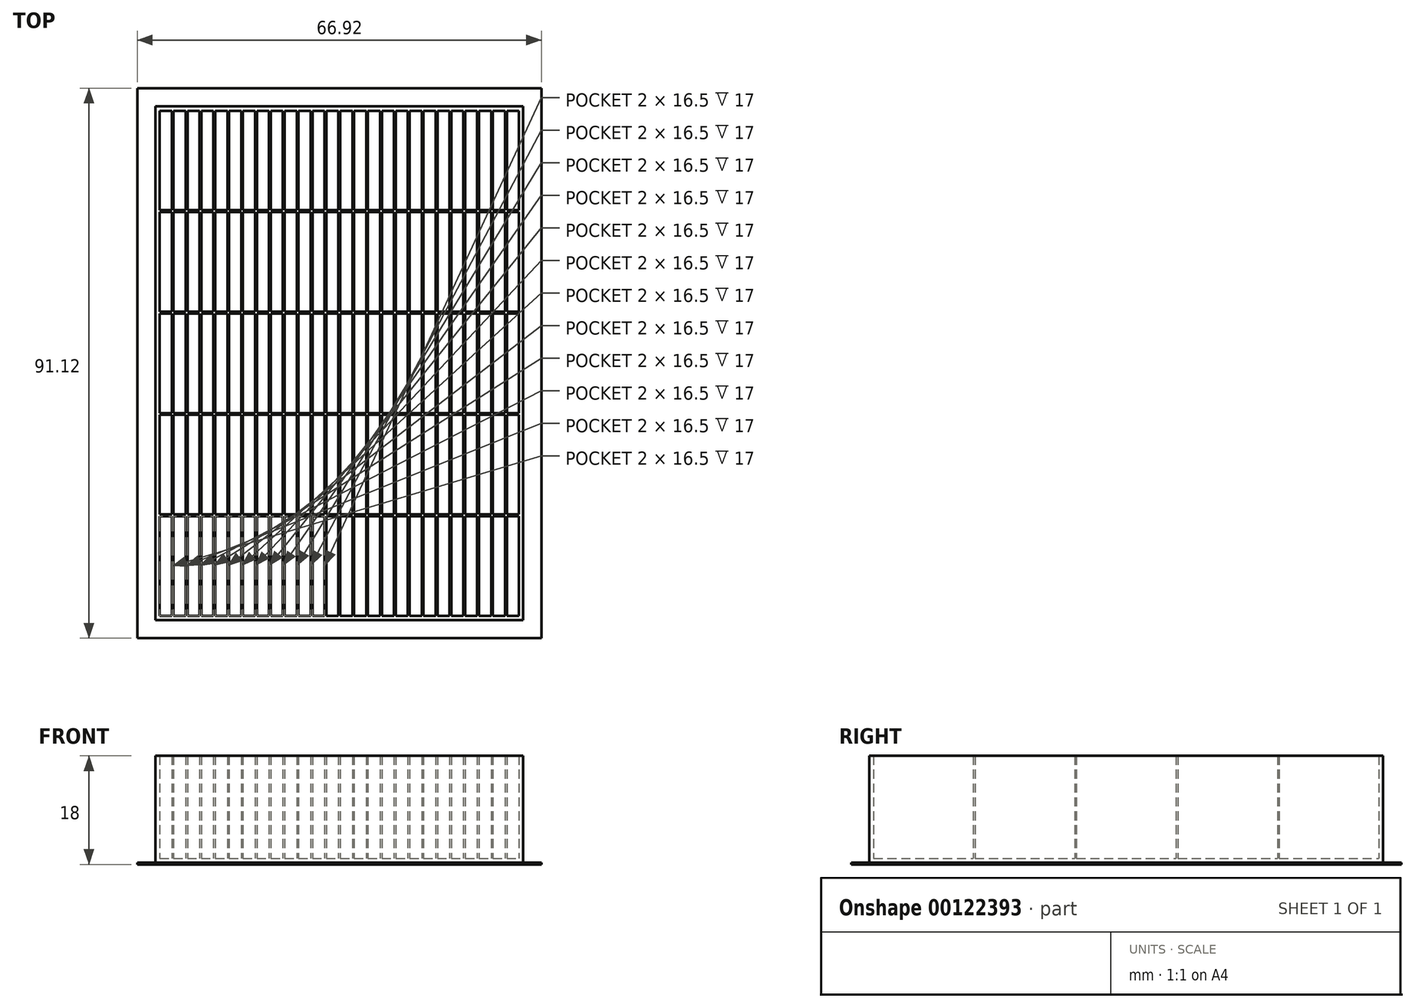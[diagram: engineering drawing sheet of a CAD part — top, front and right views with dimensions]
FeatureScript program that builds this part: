
annotation { "Feature Type Name" : "Feature", "Feature Type Description" : "" }
export const myFeature = defineFeature(function(context is Context, id is Id, definition is map)
    precondition{}
    {
        {
            var Q0;
            Q0=qCreatedBy(makeId("Top.planeOp"),FACE);
            var sketch = newSketch(context, id + "F0", { "sketchPlane" : qUnion([Q0])});
            skLineSegment(sketch, "E0.bottom", {"start": v(42.56, -30.46) * mm, "end": v(-42.56, -30.46) * mm});
            skLineSegment(sketch, "E0.top", {"start": v(42.56, 30.46) * mm, "end": v(-42.56, 30.46) * mm});
            skLineSegment(sketch, "E0.left", {"start": v(42.56, -30.46) * mm, "end": v(42.56, 30.46) * mm});
            skLineSegment(sketch, "E0.right", {"start": v(-42.56, -30.46) * mm, "end": v(-42.56, 30.46) * mm});
            skPoint(sketch, "E0.middle", {"position": v(0, 0) * mm});
            skLineSegment(sketch, "E1.bottom", {"start": v(-41.85, 29.75) * mm, "end": v(-25.35, 29.75) * mm});
            skLineSegment(sketch, "E1.top", {"start": v(-41.85, 27.75) * mm, "end": v(-25.35, 27.75) * mm});
            skLineSegment(sketch, "E1.left", {"start": v(-41.85, 29.75) * mm, "end": v(-41.85, 27.75) * mm});
            skLineSegment(sketch, "E1.right", {"start": v(-25.35, 29.75) * mm, "end": v(-25.35, 27.75) * mm});
            skLineSegment(sketch, "E2.0.1.0", {"start": v(-41.85, 27.45) * mm, "end": v(-41.85, 25.45) * mm});
            skLineSegment(sketch, "E2.0.1.1", {"start": v(-41.85, 25.45) * mm, "end": v(-25.35, 25.45) * mm});
            skLineSegment(sketch, "E2.0.1.2", {"start": v(-41.85, 27.45) * mm, "end": v(-25.35, 27.45) * mm});
            skLineSegment(sketch, "E2.0.1.3", {"start": v(-25.35, 27.45) * mm, "end": v(-25.35, 25.45) * mm});
            skLineSegment(sketch, "E2.0.2.0", {"start": v(-41.85, 25.15) * mm, "end": v(-41.85, 23.15) * mm});
            skLineSegment(sketch, "E2.0.2.1", {"start": v(-41.85, 23.15) * mm, "end": v(-25.35, 23.15) * mm});
            skLineSegment(sketch, "E2.0.2.2", {"start": v(-41.85, 25.15) * mm, "end": v(-25.35, 25.15) * mm});
            skLineSegment(sketch, "E2.0.2.3", {"start": v(-25.35, 25.15) * mm, "end": v(-25.35, 23.15) * mm});
            skLineSegment(sketch, "E2.0.3.0", {"start": v(-41.85, 22.85) * mm, "end": v(-41.85, 20.85) * mm});
            skLineSegment(sketch, "E2.0.3.1", {"start": v(-41.85, 20.85) * mm, "end": v(-25.35, 20.85) * mm});
            skLineSegment(sketch, "E2.0.3.2", {"start": v(-41.85, 22.85) * mm, "end": v(-25.35, 22.85) * mm});
            skLineSegment(sketch, "E2.0.3.3", {"start": v(-25.35, 22.85) * mm, "end": v(-25.35, 20.85) * mm});
            skLineSegment(sketch, "E2.0.4.0", {"start": v(-41.85, 20.55) * mm, "end": v(-41.85, 18.55) * mm});
            skLineSegment(sketch, "E2.0.4.1", {"start": v(-41.85, 18.55) * mm, "end": v(-25.35, 18.55) * mm});
            skLineSegment(sketch, "E2.0.4.2", {"start": v(-41.85, 20.55) * mm, "end": v(-25.35, 20.55) * mm});
            skLineSegment(sketch, "E2.0.4.3", {"start": v(-25.35, 20.55) * mm, "end": v(-25.35, 18.55) * mm});
            skLineSegment(sketch, "E2.0.5.0", {"start": v(-41.85, 18.25) * mm, "end": v(-41.85, 16.25) * mm});
            skLineSegment(sketch, "E2.0.5.1", {"start": v(-41.85, 16.25) * mm, "end": v(-25.35, 16.25) * mm});
            skLineSegment(sketch, "E2.0.5.2", {"start": v(-41.85, 18.25) * mm, "end": v(-25.35, 18.25) * mm});
            skLineSegment(sketch, "E2.0.5.3", {"start": v(-25.35, 18.25) * mm, "end": v(-25.35, 16.25) * mm});
            skLineSegment(sketch, "E2.0.6.0", {"start": v(-41.85, 15.95) * mm, "end": v(-41.85, 13.95) * mm});
            skLineSegment(sketch, "E2.0.6.1", {"start": v(-41.85, 13.95) * mm, "end": v(-25.35, 13.95) * mm});
            skLineSegment(sketch, "E2.0.6.2", {"start": v(-41.85, 15.95) * mm, "end": v(-25.35, 15.95) * mm});
            skLineSegment(sketch, "E2.0.6.3", {"start": v(-25.35, 15.95) * mm, "end": v(-25.35, 13.95) * mm});
            skLineSegment(sketch, "E2.0.7.0", {"start": v(-41.85, 13.65) * mm, "end": v(-41.85, 11.65) * mm});
            skLineSegment(sketch, "E2.0.7.1", {"start": v(-41.85, 11.65) * mm, "end": v(-25.35, 11.65) * mm});
            skLineSegment(sketch, "E2.0.7.2", {"start": v(-41.85, 13.65) * mm, "end": v(-25.35, 13.65) * mm});
            skLineSegment(sketch, "E2.0.7.3", {"start": v(-25.35, 13.65) * mm, "end": v(-25.35, 11.65) * mm});
            skLineSegment(sketch, "E2.0.8.0", {"start": v(-41.85, 11.35) * mm, "end": v(-41.85, 9.35) * mm});
            skLineSegment(sketch, "E2.0.8.1", {"start": v(-41.85, 9.35) * mm, "end": v(-25.35, 9.35) * mm});
            skLineSegment(sketch, "E2.0.8.2", {"start": v(-41.85, 11.35) * mm, "end": v(-25.35, 11.35) * mm});
            skLineSegment(sketch, "E2.0.8.3", {"start": v(-25.35, 11.35) * mm, "end": v(-25.35, 9.35) * mm});
            skLineSegment(sketch, "E2.0.9.0", {"start": v(-41.85, 9.05) * mm, "end": v(-41.85, 7.05) * mm});
            skLineSegment(sketch, "E2.0.9.1", {"start": v(-41.85, 7.05) * mm, "end": v(-25.35, 7.05) * mm});
            skLineSegment(sketch, "E2.0.9.2", {"start": v(-41.85, 9.05) * mm, "end": v(-25.35, 9.05) * mm});
            skLineSegment(sketch, "E2.0.9.3", {"start": v(-25.35, 9.05) * mm, "end": v(-25.35, 7.05) * mm});
            skLineSegment(sketch, "E2.0.10.0", {"start": v(-41.85, 6.75) * mm, "end": v(-41.85, 4.75) * mm});
            skLineSegment(sketch, "E2.0.10.1", {"start": v(-41.85, 4.75) * mm, "end": v(-25.35, 4.75) * mm});
            skLineSegment(sketch, "E2.0.10.2", {"start": v(-41.85, 6.75) * mm, "end": v(-25.35, 6.75) * mm});
            skLineSegment(sketch, "E2.0.10.3", {"start": v(-25.35, 6.75) * mm, "end": v(-25.35, 4.75) * mm});
            skLineSegment(sketch, "E2.0.11.0", {"start": v(-41.85, 4.45) * mm, "end": v(-41.85, 2.45) * mm});
            skLineSegment(sketch, "E2.0.11.1", {"start": v(-41.85, 2.45) * mm, "end": v(-25.35, 2.45) * mm});
            skLineSegment(sketch, "E2.0.11.2", {"start": v(-41.85, 4.45) * mm, "end": v(-25.35, 4.45) * mm});
            skLineSegment(sketch, "E2.0.11.3", {"start": v(-25.35, 4.45) * mm, "end": v(-25.35, 2.45) * mm});
            skLineSegment(sketch, "E2.0.12.0", {"start": v(-41.85, 2.15) * mm, "end": v(-41.85, 0.15) * mm});
            skLineSegment(sketch, "E2.0.12.1", {"start": v(-41.85, 0.15) * mm, "end": v(-25.35, 0.15) * mm});
            skLineSegment(sketch, "E2.0.12.2", {"start": v(-41.85, 2.15) * mm, "end": v(-25.35, 2.15) * mm});
            skLineSegment(sketch, "E2.0.12.3", {"start": v(-25.35, 2.15) * mm, "end": v(-25.35, 0.15) * mm});
            skLineSegment(sketch, "E2.0.13.0", {"start": v(-41.85, -0.15) * mm, "end": v(-41.85, -2.15) * mm});
            skLineSegment(sketch, "E2.0.13.1", {"start": v(-41.85, -2.15) * mm, "end": v(-25.35, -2.15) * mm});
            skLineSegment(sketch, "E2.0.13.2", {"start": v(-41.85, -0.15) * mm, "end": v(-25.35, -0.15) * mm});
            skLineSegment(sketch, "E2.0.13.3", {"start": v(-25.35, -0.15) * mm, "end": v(-25.35, -2.15) * mm});
            skLineSegment(sketch, "E2.0.14.0", {"start": v(-41.85, -2.45) * mm, "end": v(-41.85, -4.45) * mm});
            skLineSegment(sketch, "E2.0.14.1", {"start": v(-41.85, -4.45) * mm, "end": v(-25.35, -4.45) * mm});
            skLineSegment(sketch, "E2.0.14.2", {"start": v(-41.85, -2.45) * mm, "end": v(-25.35, -2.45) * mm});
            skLineSegment(sketch, "E2.0.14.3", {"start": v(-25.35, -2.45) * mm, "end": v(-25.35, -4.45) * mm});
            skLineSegment(sketch, "E2.0.15.0", {"start": v(-41.85, -4.75) * mm, "end": v(-41.85, -6.75) * mm});
            skLineSegment(sketch, "E2.0.15.1", {"start": v(-41.85, -6.75) * mm, "end": v(-25.35, -6.75) * mm});
            skLineSegment(sketch, "E2.0.15.2", {"start": v(-41.85, -4.75) * mm, "end": v(-25.35, -4.75) * mm});
            skLineSegment(sketch, "E2.0.15.3", {"start": v(-25.35, -4.75) * mm, "end": v(-25.35, -6.75) * mm});
            skLineSegment(sketch, "E2.0.16.0", {"start": v(-41.85, -7.05) * mm, "end": v(-41.85, -9.05) * mm});
            skLineSegment(sketch, "E2.0.16.1", {"start": v(-41.85, -9.05) * mm, "end": v(-25.35, -9.05) * mm});
            skLineSegment(sketch, "E2.0.16.2", {"start": v(-41.85, -7.05) * mm, "end": v(-25.35, -7.05) * mm});
            skLineSegment(sketch, "E2.0.16.3", {"start": v(-25.35, -7.05) * mm, "end": v(-25.35, -9.05) * mm});
            skLineSegment(sketch, "E2.0.17.0", {"start": v(-41.85, -9.35) * mm, "end": v(-41.85, -11.35) * mm});
            skLineSegment(sketch, "E2.0.17.1", {"start": v(-41.85, -11.35) * mm, "end": v(-25.35, -11.35) * mm});
            skLineSegment(sketch, "E2.0.17.2", {"start": v(-41.85, -9.35) * mm, "end": v(-25.35, -9.35) * mm});
            skLineSegment(sketch, "E2.0.17.3", {"start": v(-25.35, -9.35) * mm, "end": v(-25.35, -11.35) * mm});
            skLineSegment(sketch, "E2.0.18.0", {"start": v(-41.85, -11.65) * mm, "end": v(-41.85, -13.65) * mm});
            skLineSegment(sketch, "E2.0.18.1", {"start": v(-41.85, -13.65) * mm, "end": v(-25.35, -13.65) * mm});
            skLineSegment(sketch, "E2.0.18.2", {"start": v(-41.85, -11.65) * mm, "end": v(-25.35, -11.65) * mm});
            skLineSegment(sketch, "E2.0.18.3", {"start": v(-25.35, -11.65) * mm, "end": v(-25.35, -13.65) * mm});
            skLineSegment(sketch, "E2.0.19.0", {"start": v(-41.85, -13.95) * mm, "end": v(-41.85, -15.95) * mm});
            skLineSegment(sketch, "E2.0.19.1", {"start": v(-41.85, -15.95) * mm, "end": v(-25.35, -15.95) * mm});
            skLineSegment(sketch, "E2.0.19.2", {"start": v(-41.85, -13.95) * mm, "end": v(-25.35, -13.95) * mm});
            skLineSegment(sketch, "E2.0.19.3", {"start": v(-25.35, -13.95) * mm, "end": v(-25.35, -15.95) * mm});
            skLineSegment(sketch, "E2.0.20.0", {"start": v(-41.85, -16.25) * mm, "end": v(-41.85, -18.25) * mm});
            skLineSegment(sketch, "E2.0.20.1", {"start": v(-41.85, -18.25) * mm, "end": v(-25.35, -18.25) * mm});
            skLineSegment(sketch, "E2.0.20.2", {"start": v(-41.85, -16.25) * mm, "end": v(-25.35, -16.25) * mm});
            skLineSegment(sketch, "E2.0.20.3", {"start": v(-25.35, -16.25) * mm, "end": v(-25.35, -18.25) * mm});
            skLineSegment(sketch, "E2.0.21.0", {"start": v(-41.85, -18.55) * mm, "end": v(-41.85, -20.55) * mm});
            skLineSegment(sketch, "E2.0.21.1", {"start": v(-41.85, -20.55) * mm, "end": v(-25.35, -20.55) * mm});
            skLineSegment(sketch, "E2.0.21.2", {"start": v(-41.85, -18.55) * mm, "end": v(-25.35, -18.55) * mm});
            skLineSegment(sketch, "E2.0.21.3", {"start": v(-25.35, -18.55) * mm, "end": v(-25.35, -20.55) * mm});
            skLineSegment(sketch, "E2.0.22.0", {"start": v(-41.85, -20.85) * mm, "end": v(-41.85, -22.85) * mm});
            skLineSegment(sketch, "E2.0.22.1", {"start": v(-41.85, -22.85) * mm, "end": v(-25.35, -22.85) * mm});
            skLineSegment(sketch, "E2.0.22.2", {"start": v(-41.85, -20.85) * mm, "end": v(-25.35, -20.85) * mm});
            skLineSegment(sketch, "E2.0.22.3", {"start": v(-25.35, -20.85) * mm, "end": v(-25.35, -22.85) * mm});
            skLineSegment(sketch, "E2.0.23.0", {"start": v(-41.85, -23.15) * mm, "end": v(-41.85, -25.15) * mm});
            skLineSegment(sketch, "E2.0.23.1", {"start": v(-41.85, -25.15) * mm, "end": v(-25.35, -25.15) * mm});
            skLineSegment(sketch, "E2.0.23.2", {"start": v(-41.85, -23.15) * mm, "end": v(-25.35, -23.15) * mm});
            skLineSegment(sketch, "E2.0.23.3", {"start": v(-25.35, -23.15) * mm, "end": v(-25.35, -25.15) * mm});
            skLineSegment(sketch, "E2.0.24.0", {"start": v(-41.85, -25.45) * mm, "end": v(-41.85, -27.45) * mm});
            skLineSegment(sketch, "E2.0.24.1", {"start": v(-41.85, -27.45) * mm, "end": v(-25.35, -27.45) * mm});
            skLineSegment(sketch, "E2.0.24.2", {"start": v(-41.85, -25.45) * mm, "end": v(-25.35, -25.45) * mm});
            skLineSegment(sketch, "E2.0.24.3", {"start": v(-25.35, -25.45) * mm, "end": v(-25.35, -27.45) * mm});
            skLineSegment(sketch, "E2.0.25.0", {"start": v(-41.85, -27.75) * mm, "end": v(-41.85, -29.75) * mm});
            skLineSegment(sketch, "E2.0.25.1", {"start": v(-41.85, -29.75) * mm, "end": v(-25.35, -29.75) * mm});
            skLineSegment(sketch, "E2.0.25.2", {"start": v(-41.85, -27.75) * mm, "end": v(-25.35, -27.75) * mm});
            skLineSegment(sketch, "E2.0.25.3", {"start": v(-25.35, -27.75) * mm, "end": v(-25.35, -29.75) * mm});
            skLineSegment(sketch, "E2.1.0.0", {"start": v(-25.05, 29.75) * mm, "end": v(-25.05, 27.75) * mm});
            skLineSegment(sketch, "E2.1.0.1", {"start": v(-25.05, 27.75) * mm, "end": v(-8.55, 27.75) * mm});
            skLineSegment(sketch, "E2.1.0.2", {"start": v(-25.05, 29.75) * mm, "end": v(-8.55, 29.75) * mm});
            skLineSegment(sketch, "E2.1.0.3", {"start": v(-8.55, 29.75) * mm, "end": v(-8.55, 27.75) * mm});
            skLineSegment(sketch, "E2.1.1.0", {"start": v(-25.05, 27.45) * mm, "end": v(-25.05, 25.45) * mm});
            skLineSegment(sketch, "E2.1.1.1", {"start": v(-25.05, 25.45) * mm, "end": v(-8.55, 25.45) * mm});
            skLineSegment(sketch, "E2.1.1.2", {"start": v(-25.05, 27.45) * mm, "end": v(-8.55, 27.45) * mm});
            skLineSegment(sketch, "E2.1.1.3", {"start": v(-8.55, 27.45) * mm, "end": v(-8.55, 25.45) * mm});
            skLineSegment(sketch, "E2.1.2.0", {"start": v(-25.05, 25.15) * mm, "end": v(-25.05, 23.15) * mm});
            skLineSegment(sketch, "E2.1.2.1", {"start": v(-25.05, 23.15) * mm, "end": v(-8.55, 23.15) * mm});
            skLineSegment(sketch, "E2.1.2.2", {"start": v(-25.05, 25.15) * mm, "end": v(-8.55, 25.15) * mm});
            skLineSegment(sketch, "E2.1.2.3", {"start": v(-8.55, 25.15) * mm, "end": v(-8.55, 23.15) * mm});
            skLineSegment(sketch, "E2.1.3.0", {"start": v(-25.05, 22.85) * mm, "end": v(-25.05, 20.85) * mm});
            skLineSegment(sketch, "E2.1.3.1", {"start": v(-25.05, 20.85) * mm, "end": v(-8.55, 20.85) * mm});
            skLineSegment(sketch, "E2.1.3.2", {"start": v(-25.05, 22.85) * mm, "end": v(-8.55, 22.85) * mm});
            skLineSegment(sketch, "E2.1.3.3", {"start": v(-8.55, 22.85) * mm, "end": v(-8.55, 20.85) * mm});
            skLineSegment(sketch, "E2.1.4.0", {"start": v(-25.05, 20.55) * mm, "end": v(-25.05, 18.55) * mm});
            skLineSegment(sketch, "E2.1.4.1", {"start": v(-25.05, 18.55) * mm, "end": v(-8.55, 18.55) * mm});
            skLineSegment(sketch, "E2.1.4.2", {"start": v(-25.05, 20.55) * mm, "end": v(-8.55, 20.55) * mm});
            skLineSegment(sketch, "E2.1.4.3", {"start": v(-8.55, 20.55) * mm, "end": v(-8.55, 18.55) * mm});
            skLineSegment(sketch, "E2.1.5.0", {"start": v(-25.05, 18.25) * mm, "end": v(-25.05, 16.25) * mm});
            skLineSegment(sketch, "E2.1.5.1", {"start": v(-25.05, 16.25) * mm, "end": v(-8.55, 16.25) * mm});
            skLineSegment(sketch, "E2.1.5.2", {"start": v(-25.05, 18.25) * mm, "end": v(-8.55, 18.25) * mm});
            skLineSegment(sketch, "E2.1.5.3", {"start": v(-8.55, 18.25) * mm, "end": v(-8.55, 16.25) * mm});
            skLineSegment(sketch, "E2.1.6.0", {"start": v(-25.05, 15.95) * mm, "end": v(-25.05, 13.95) * mm});
            skLineSegment(sketch, "E2.1.6.1", {"start": v(-25.05, 13.95) * mm, "end": v(-8.55, 13.95) * mm});
            skLineSegment(sketch, "E2.1.6.2", {"start": v(-25.05, 15.95) * mm, "end": v(-8.55, 15.95) * mm});
            skLineSegment(sketch, "E2.1.6.3", {"start": v(-8.55, 15.95) * mm, "end": v(-8.55, 13.95) * mm});
            skLineSegment(sketch, "E2.1.7.0", {"start": v(-25.05, 13.65) * mm, "end": v(-25.05, 11.65) * mm});
            skLineSegment(sketch, "E2.1.7.1", {"start": v(-25.05, 11.65) * mm, "end": v(-8.55, 11.65) * mm});
            skLineSegment(sketch, "E2.1.7.2", {"start": v(-25.05, 13.65) * mm, "end": v(-8.55, 13.65) * mm});
            skLineSegment(sketch, "E2.1.7.3", {"start": v(-8.55, 13.65) * mm, "end": v(-8.55, 11.65) * mm});
            skLineSegment(sketch, "E2.1.8.0", {"start": v(-25.05, 11.35) * mm, "end": v(-25.05, 9.35) * mm});
            skLineSegment(sketch, "E2.1.8.1", {"start": v(-25.05, 9.35) * mm, "end": v(-8.55, 9.35) * mm});
            skLineSegment(sketch, "E2.1.8.2", {"start": v(-25.05, 11.35) * mm, "end": v(-8.55, 11.35) * mm});
            skLineSegment(sketch, "E2.1.8.3", {"start": v(-8.55, 11.35) * mm, "end": v(-8.55, 9.35) * mm});
            skLineSegment(sketch, "E2.1.9.0", {"start": v(-25.05, 9.05) * mm, "end": v(-25.05, 7.05) * mm});
            skLineSegment(sketch, "E2.1.9.1", {"start": v(-25.05, 7.05) * mm, "end": v(-8.55, 7.05) * mm});
            skLineSegment(sketch, "E2.1.9.2", {"start": v(-25.05, 9.05) * mm, "end": v(-8.55, 9.05) * mm});
            skLineSegment(sketch, "E2.1.9.3", {"start": v(-8.55, 9.05) * mm, "end": v(-8.55, 7.05) * mm});
            skLineSegment(sketch, "E2.1.10.0", {"start": v(-25.05, 6.75) * mm, "end": v(-25.05, 4.75) * mm});
            skLineSegment(sketch, "E2.1.10.1", {"start": v(-25.05, 4.75) * mm, "end": v(-8.55, 4.75) * mm});
            skLineSegment(sketch, "E2.1.10.2", {"start": v(-25.05, 6.75) * mm, "end": v(-8.55, 6.75) * mm});
            skLineSegment(sketch, "E2.1.10.3", {"start": v(-8.55, 6.75) * mm, "end": v(-8.55, 4.75) * mm});
            skLineSegment(sketch, "E2.1.11.0", {"start": v(-25.05, 4.45) * mm, "end": v(-25.05, 2.45) * mm});
            skLineSegment(sketch, "E2.1.11.1", {"start": v(-25.05, 2.45) * mm, "end": v(-8.55, 2.45) * mm});
            skLineSegment(sketch, "E2.1.11.2", {"start": v(-25.05, 4.45) * mm, "end": v(-8.55, 4.45) * mm});
            skLineSegment(sketch, "E2.1.11.3", {"start": v(-8.55, 4.45) * mm, "end": v(-8.55, 2.45) * mm});
            skLineSegment(sketch, "E2.1.12.0", {"start": v(-25.05, 2.15) * mm, "end": v(-25.05, 0.15) * mm});
            skLineSegment(sketch, "E2.1.12.1", {"start": v(-25.05, 0.15) * mm, "end": v(-8.55, 0.15) * mm});
            skLineSegment(sketch, "E2.1.12.2", {"start": v(-25.05, 2.15) * mm, "end": v(-8.55, 2.15) * mm});
            skLineSegment(sketch, "E2.1.12.3", {"start": v(-8.55, 2.15) * mm, "end": v(-8.55, 0.15) * mm});
            skLineSegment(sketch, "E2.1.13.0", {"start": v(-25.05, -0.15) * mm, "end": v(-25.05, -2.15) * mm});
            skLineSegment(sketch, "E2.1.13.1", {"start": v(-25.05, -2.15) * mm, "end": v(-8.55, -2.15) * mm});
            skLineSegment(sketch, "E2.1.13.2", {"start": v(-25.05, -0.15) * mm, "end": v(-8.55, -0.15) * mm});
            skLineSegment(sketch, "E2.1.13.3", {"start": v(-8.55, -0.15) * mm, "end": v(-8.55, -2.15) * mm});
            skLineSegment(sketch, "E2.1.14.0", {"start": v(-25.05, -2.45) * mm, "end": v(-25.05, -4.45) * mm});
            skLineSegment(sketch, "E2.1.14.1", {"start": v(-25.05, -4.45) * mm, "end": v(-8.55, -4.45) * mm});
            skLineSegment(sketch, "E2.1.14.2", {"start": v(-25.05, -2.45) * mm, "end": v(-8.55, -2.45) * mm});
            skLineSegment(sketch, "E2.1.14.3", {"start": v(-8.55, -2.45) * mm, "end": v(-8.55, -4.45) * mm});
            skLineSegment(sketch, "E2.1.15.0", {"start": v(-25.05, -4.75) * mm, "end": v(-25.05, -6.75) * mm});
            skLineSegment(sketch, "E2.1.15.1", {"start": v(-25.05, -6.75) * mm, "end": v(-8.55, -6.75) * mm});
            skLineSegment(sketch, "E2.1.15.2", {"start": v(-25.05, -4.75) * mm, "end": v(-8.55, -4.75) * mm});
            skLineSegment(sketch, "E2.1.15.3", {"start": v(-8.55, -4.75) * mm, "end": v(-8.55, -6.75) * mm});
            skLineSegment(sketch, "E2.1.16.0", {"start": v(-25.05, -7.05) * mm, "end": v(-25.05, -9.05) * mm});
            skLineSegment(sketch, "E2.1.16.1", {"start": v(-25.05, -9.05) * mm, "end": v(-8.55, -9.05) * mm});
            skLineSegment(sketch, "E2.1.16.2", {"start": v(-25.05, -7.05) * mm, "end": v(-8.55, -7.05) * mm});
            skLineSegment(sketch, "E2.1.16.3", {"start": v(-8.55, -7.05) * mm, "end": v(-8.55, -9.05) * mm});
            skLineSegment(sketch, "E2.1.17.0", {"start": v(-25.05, -9.35) * mm, "end": v(-25.05, -11.35) * mm});
            skLineSegment(sketch, "E2.1.17.1", {"start": v(-25.05, -11.35) * mm, "end": v(-8.55, -11.35) * mm});
            skLineSegment(sketch, "E2.1.17.2", {"start": v(-25.05, -9.35) * mm, "end": v(-8.55, -9.35) * mm});
            skLineSegment(sketch, "E2.1.17.3", {"start": v(-8.55, -9.35) * mm, "end": v(-8.55, -11.35) * mm});
            skLineSegment(sketch, "E2.1.18.0", {"start": v(-25.05, -11.65) * mm, "end": v(-25.05, -13.65) * mm});
            skLineSegment(sketch, "E2.1.18.1", {"start": v(-25.05, -13.65) * mm, "end": v(-8.55, -13.65) * mm});
            skLineSegment(sketch, "E2.1.18.2", {"start": v(-25.05, -11.65) * mm, "end": v(-8.55, -11.65) * mm});
            skLineSegment(sketch, "E2.1.18.3", {"start": v(-8.55, -11.65) * mm, "end": v(-8.55, -13.65) * mm});
            skLineSegment(sketch, "E2.1.19.0", {"start": v(-25.05, -13.95) * mm, "end": v(-25.05, -15.95) * mm});
            skLineSegment(sketch, "E2.1.19.1", {"start": v(-25.05, -15.95) * mm, "end": v(-8.55, -15.95) * mm});
            skLineSegment(sketch, "E2.1.19.2", {"start": v(-25.05, -13.95) * mm, "end": v(-8.55, -13.95) * mm});
            skLineSegment(sketch, "E2.1.19.3", {"start": v(-8.55, -13.95) * mm, "end": v(-8.55, -15.95) * mm});
            skLineSegment(sketch, "E2.1.20.0", {"start": v(-25.05, -16.25) * mm, "end": v(-25.05, -18.25) * mm});
            skLineSegment(sketch, "E2.1.20.1", {"start": v(-25.05, -18.25) * mm, "end": v(-8.55, -18.25) * mm});
            skLineSegment(sketch, "E2.1.20.2", {"start": v(-25.05, -16.25) * mm, "end": v(-8.55, -16.25) * mm});
            skLineSegment(sketch, "E2.1.20.3", {"start": v(-8.55, -16.25) * mm, "end": v(-8.55, -18.25) * mm});
            skLineSegment(sketch, "E2.1.21.0", {"start": v(-25.05, -18.55) * mm, "end": v(-25.05, -20.55) * mm});
            skLineSegment(sketch, "E2.1.21.1", {"start": v(-25.05, -20.55) * mm, "end": v(-8.55, -20.55) * mm});
            skLineSegment(sketch, "E2.1.21.2", {"start": v(-25.05, -18.55) * mm, "end": v(-8.55, -18.55) * mm});
            skLineSegment(sketch, "E2.1.21.3", {"start": v(-8.55, -18.55) * mm, "end": v(-8.55, -20.55) * mm});
            skLineSegment(sketch, "E2.1.22.0", {"start": v(-25.05, -20.85) * mm, "end": v(-25.05, -22.85) * mm});
            skLineSegment(sketch, "E2.1.22.1", {"start": v(-25.05, -22.85) * mm, "end": v(-8.55, -22.85) * mm});
            skLineSegment(sketch, "E2.1.22.2", {"start": v(-25.05, -20.85) * mm, "end": v(-8.55, -20.85) * mm});
            skLineSegment(sketch, "E2.1.22.3", {"start": v(-8.55, -20.85) * mm, "end": v(-8.55, -22.85) * mm});
            skLineSegment(sketch, "E2.1.23.0", {"start": v(-25.05, -23.15) * mm, "end": v(-25.05, -25.15) * mm});
            skLineSegment(sketch, "E2.1.23.1", {"start": v(-25.05, -25.15) * mm, "end": v(-8.55, -25.15) * mm});
            skLineSegment(sketch, "E2.1.23.2", {"start": v(-25.05, -23.15) * mm, "end": v(-8.55, -23.15) * mm});
            skLineSegment(sketch, "E2.1.23.3", {"start": v(-8.55, -23.15) * mm, "end": v(-8.55, -25.15) * mm});
            skLineSegment(sketch, "E2.1.24.0", {"start": v(-25.05, -25.45) * mm, "end": v(-25.05, -27.45) * mm});
            skLineSegment(sketch, "E2.1.24.1", {"start": v(-25.05, -27.45) * mm, "end": v(-8.55, -27.45) * mm});
            skLineSegment(sketch, "E2.1.24.2", {"start": v(-25.05, -25.45) * mm, "end": v(-8.55, -25.45) * mm});
            skLineSegment(sketch, "E2.1.24.3", {"start": v(-8.55, -25.45) * mm, "end": v(-8.55, -27.45) * mm});
            skLineSegment(sketch, "E2.1.25.0", {"start": v(-25.05, -27.75) * mm, "end": v(-25.05, -29.75) * mm});
            skLineSegment(sketch, "E2.1.25.1", {"start": v(-25.05, -29.75) * mm, "end": v(-8.55, -29.75) * mm});
            skLineSegment(sketch, "E2.1.25.2", {"start": v(-25.05, -27.75) * mm, "end": v(-8.55, -27.75) * mm});
            skLineSegment(sketch, "E2.1.25.3", {"start": v(-8.55, -27.75) * mm, "end": v(-8.55, -29.75) * mm});
            skLineSegment(sketch, "E2.2.0.0", {"start": v(-8.25, 29.75) * mm, "end": v(-8.25, 27.75) * mm});
            skLineSegment(sketch, "E2.2.0.1", {"start": v(-8.25, 27.75) * mm, "end": v(8.25, 27.75) * mm});
            skLineSegment(sketch, "E2.2.0.2", {"start": v(-8.25, 29.75) * mm, "end": v(8.25, 29.75) * mm});
            skLineSegment(sketch, "E2.2.0.3", {"start": v(8.25, 29.75) * mm, "end": v(8.25, 27.75) * mm});
            skLineSegment(sketch, "E2.2.1.0", {"start": v(-8.25, 27.45) * mm, "end": v(-8.25, 25.45) * mm});
            skLineSegment(sketch, "E2.2.1.1", {"start": v(-8.25, 25.45) * mm, "end": v(8.25, 25.45) * mm});
            skLineSegment(sketch, "E2.2.1.2", {"start": v(-8.25, 27.45) * mm, "end": v(8.25, 27.45) * mm});
            skLineSegment(sketch, "E2.2.1.3", {"start": v(8.25, 27.45) * mm, "end": v(8.25, 25.45) * mm});
            skLineSegment(sketch, "E2.2.2.0", {"start": v(-8.25, 25.15) * mm, "end": v(-8.25, 23.15) * mm});
            skLineSegment(sketch, "E2.2.2.1", {"start": v(-8.25, 23.15) * mm, "end": v(8.25, 23.15) * mm});
            skLineSegment(sketch, "E2.2.2.2", {"start": v(-8.25, 25.15) * mm, "end": v(8.25, 25.15) * mm});
            skLineSegment(sketch, "E2.2.2.3", {"start": v(8.25, 25.15) * mm, "end": v(8.25, 23.15) * mm});
            skLineSegment(sketch, "E2.2.3.0", {"start": v(-8.25, 22.85) * mm, "end": v(-8.25, 20.85) * mm});
            skLineSegment(sketch, "E2.2.3.1", {"start": v(-8.25, 20.85) * mm, "end": v(8.25, 20.85) * mm});
            skLineSegment(sketch, "E2.2.3.2", {"start": v(-8.25, 22.85) * mm, "end": v(8.25, 22.85) * mm});
            skLineSegment(sketch, "E2.2.3.3", {"start": v(8.25, 22.85) * mm, "end": v(8.25, 20.85) * mm});
            skLineSegment(sketch, "E2.2.4.0", {"start": v(-8.25, 20.55) * mm, "end": v(-8.25, 18.55) * mm});
            skLineSegment(sketch, "E2.2.4.1", {"start": v(-8.25, 18.55) * mm, "end": v(8.25, 18.55) * mm});
            skLineSegment(sketch, "E2.2.4.2", {"start": v(-8.25, 20.55) * mm, "end": v(8.25, 20.55) * mm});
            skLineSegment(sketch, "E2.2.4.3", {"start": v(8.25, 20.55) * mm, "end": v(8.25, 18.55) * mm});
            skLineSegment(sketch, "E2.2.5.0", {"start": v(-8.25, 18.25) * mm, "end": v(-8.25, 16.25) * mm});
            skLineSegment(sketch, "E2.2.5.1", {"start": v(-8.25, 16.25) * mm, "end": v(8.25, 16.25) * mm});
            skLineSegment(sketch, "E2.2.5.2", {"start": v(-8.25, 18.25) * mm, "end": v(8.25, 18.25) * mm});
            skLineSegment(sketch, "E2.2.5.3", {"start": v(8.25, 18.25) * mm, "end": v(8.25, 16.25) * mm});
            skLineSegment(sketch, "E2.2.6.0", {"start": v(-8.25, 15.95) * mm, "end": v(-8.25, 13.95) * mm});
            skLineSegment(sketch, "E2.2.6.1", {"start": v(-8.25, 13.95) * mm, "end": v(8.25, 13.95) * mm});
            skLineSegment(sketch, "E2.2.6.2", {"start": v(-8.25, 15.95) * mm, "end": v(8.25, 15.95) * mm});
            skLineSegment(sketch, "E2.2.6.3", {"start": v(8.25, 15.95) * mm, "end": v(8.25, 13.95) * mm});
            skLineSegment(sketch, "E2.2.7.0", {"start": v(-8.25, 13.65) * mm, "end": v(-8.25, 11.65) * mm});
            skLineSegment(sketch, "E2.2.7.1", {"start": v(-8.25, 11.65) * mm, "end": v(8.25, 11.65) * mm});
            skLineSegment(sketch, "E2.2.7.2", {"start": v(-8.25, 13.65) * mm, "end": v(8.25, 13.65) * mm});
            skLineSegment(sketch, "E2.2.7.3", {"start": v(8.25, 13.65) * mm, "end": v(8.25, 11.65) * mm});
            skLineSegment(sketch, "E2.2.8.0", {"start": v(-8.25, 11.35) * mm, "end": v(-8.25, 9.35) * mm});
            skLineSegment(sketch, "E2.2.8.1", {"start": v(-8.25, 9.35) * mm, "end": v(8.25, 9.35) * mm});
            skLineSegment(sketch, "E2.2.8.2", {"start": v(-8.25, 11.35) * mm, "end": v(8.25, 11.35) * mm});
            skLineSegment(sketch, "E2.2.8.3", {"start": v(8.25, 11.35) * mm, "end": v(8.25, 9.35) * mm});
            skLineSegment(sketch, "E2.2.9.0", {"start": v(-8.25, 9.05) * mm, "end": v(-8.25, 7.05) * mm});
            skLineSegment(sketch, "E2.2.9.1", {"start": v(-8.25, 7.05) * mm, "end": v(8.25, 7.05) * mm});
            skLineSegment(sketch, "E2.2.9.2", {"start": v(-8.25, 9.05) * mm, "end": v(8.25, 9.05) * mm});
            skLineSegment(sketch, "E2.2.9.3", {"start": v(8.25, 9.05) * mm, "end": v(8.25, 7.05) * mm});
            skLineSegment(sketch, "E2.2.10.0", {"start": v(-8.25, 6.75) * mm, "end": v(-8.25, 4.75) * mm});
            skLineSegment(sketch, "E2.2.10.1", {"start": v(-8.25, 4.75) * mm, "end": v(8.25, 4.75) * mm});
            skLineSegment(sketch, "E2.2.10.2", {"start": v(-8.25, 6.75) * mm, "end": v(8.25, 6.75) * mm});
            skLineSegment(sketch, "E2.2.10.3", {"start": v(8.25, 6.75) * mm, "end": v(8.25, 4.75) * mm});
            skLineSegment(sketch, "E2.2.11.0", {"start": v(-8.25, 4.45) * mm, "end": v(-8.25, 2.45) * mm});
            skLineSegment(sketch, "E2.2.11.1", {"start": v(-8.25, 2.45) * mm, "end": v(8.25, 2.45) * mm});
            skLineSegment(sketch, "E2.2.11.2", {"start": v(-8.25, 4.45) * mm, "end": v(8.25, 4.45) * mm});
            skLineSegment(sketch, "E2.2.11.3", {"start": v(8.25, 4.45) * mm, "end": v(8.25, 2.45) * mm});
            skLineSegment(sketch, "E2.2.12.0", {"start": v(-8.25, 2.15) * mm, "end": v(-8.25, 0.15) * mm});
            skLineSegment(sketch, "E2.2.12.1", {"start": v(-8.25, 0.15) * mm, "end": v(8.25, 0.15) * mm});
            skLineSegment(sketch, "E2.2.12.2", {"start": v(-8.25, 2.15) * mm, "end": v(8.25, 2.15) * mm});
            skLineSegment(sketch, "E2.2.12.3", {"start": v(8.25, 2.15) * mm, "end": v(8.25, 0.15) * mm});
            skLineSegment(sketch, "E2.2.13.0", {"start": v(-8.25, -0.15) * mm, "end": v(-8.25, -2.15) * mm});
            skLineSegment(sketch, "E2.2.13.1", {"start": v(-8.25, -2.15) * mm, "end": v(8.25, -2.15) * mm});
            skLineSegment(sketch, "E2.2.13.2", {"start": v(-8.25, -0.15) * mm, "end": v(8.25, -0.15) * mm});
            skLineSegment(sketch, "E2.2.13.3", {"start": v(8.25, -0.15) * mm, "end": v(8.25, -2.15) * mm});
            skLineSegment(sketch, "E2.2.14.0", {"start": v(-8.25, -2.45) * mm, "end": v(-8.25, -4.45) * mm});
            skLineSegment(sketch, "E2.2.14.1", {"start": v(-8.25, -4.45) * mm, "end": v(8.25, -4.45) * mm});
            skLineSegment(sketch, "E2.2.14.2", {"start": v(-8.25, -2.45) * mm, "end": v(8.25, -2.45) * mm});
            skLineSegment(sketch, "E2.2.14.3", {"start": v(8.25, -2.45) * mm, "end": v(8.25, -4.45) * mm});
            skLineSegment(sketch, "E2.2.15.0", {"start": v(-8.25, -4.75) * mm, "end": v(-8.25, -6.75) * mm});
            skLineSegment(sketch, "E2.2.15.1", {"start": v(-8.25, -6.75) * mm, "end": v(8.25, -6.75) * mm});
            skLineSegment(sketch, "E2.2.15.2", {"start": v(-8.25, -4.75) * mm, "end": v(8.25, -4.75) * mm});
            skLineSegment(sketch, "E2.2.15.3", {"start": v(8.25, -4.75) * mm, "end": v(8.25, -6.75) * mm});
            skLineSegment(sketch, "E2.2.16.0", {"start": v(-8.25, -7.05) * mm, "end": v(-8.25, -9.05) * mm});
            skLineSegment(sketch, "E2.2.16.1", {"start": v(-8.25, -9.05) * mm, "end": v(8.25, -9.05) * mm});
            skLineSegment(sketch, "E2.2.16.2", {"start": v(-8.25, -7.05) * mm, "end": v(8.25, -7.05) * mm});
            skLineSegment(sketch, "E2.2.16.3", {"start": v(8.25, -7.05) * mm, "end": v(8.25, -9.05) * mm});
            skLineSegment(sketch, "E2.2.17.0", {"start": v(-8.25, -9.35) * mm, "end": v(-8.25, -11.35) * mm});
            skLineSegment(sketch, "E2.2.17.1", {"start": v(-8.25, -11.35) * mm, "end": v(8.25, -11.35) * mm});
            skLineSegment(sketch, "E2.2.17.2", {"start": v(-8.25, -9.35) * mm, "end": v(8.25, -9.35) * mm});
            skLineSegment(sketch, "E2.2.17.3", {"start": v(8.25, -9.35) * mm, "end": v(8.25, -11.35) * mm});
            skLineSegment(sketch, "E2.2.18.0", {"start": v(-8.25, -11.65) * mm, "end": v(-8.25, -13.65) * mm});
            skLineSegment(sketch, "E2.2.18.1", {"start": v(-8.25, -13.65) * mm, "end": v(8.25, -13.65) * mm});
            skLineSegment(sketch, "E2.2.18.2", {"start": v(-8.25, -11.65) * mm, "end": v(8.25, -11.65) * mm});
            skLineSegment(sketch, "E2.2.18.3", {"start": v(8.25, -11.65) * mm, "end": v(8.25, -13.65) * mm});
            skLineSegment(sketch, "E2.2.19.0", {"start": v(-8.25, -13.95) * mm, "end": v(-8.25, -15.95) * mm});
            skLineSegment(sketch, "E2.2.19.1", {"start": v(-8.25, -15.95) * mm, "end": v(8.25, -15.95) * mm});
            skLineSegment(sketch, "E2.2.19.2", {"start": v(-8.25, -13.95) * mm, "end": v(8.25, -13.95) * mm});
            skLineSegment(sketch, "E2.2.19.3", {"start": v(8.25, -13.95) * mm, "end": v(8.25, -15.95) * mm});
            skLineSegment(sketch, "E2.2.20.0", {"start": v(-8.25, -16.25) * mm, "end": v(-8.25, -18.25) * mm});
            skLineSegment(sketch, "E2.2.20.1", {"start": v(-8.25, -18.25) * mm, "end": v(8.25, -18.25) * mm});
            skLineSegment(sketch, "E2.2.20.2", {"start": v(-8.25, -16.25) * mm, "end": v(8.25, -16.25) * mm});
            skLineSegment(sketch, "E2.2.20.3", {"start": v(8.25, -16.25) * mm, "end": v(8.25, -18.25) * mm});
            skLineSegment(sketch, "E2.2.21.0", {"start": v(-8.25, -18.55) * mm, "end": v(-8.25, -20.55) * mm});
            skLineSegment(sketch, "E2.2.21.1", {"start": v(-8.25, -20.55) * mm, "end": v(8.25, -20.55) * mm});
            skLineSegment(sketch, "E2.2.21.2", {"start": v(-8.25, -18.55) * mm, "end": v(8.25, -18.55) * mm});
            skLineSegment(sketch, "E2.2.21.3", {"start": v(8.25, -18.55) * mm, "end": v(8.25, -20.55) * mm});
            skLineSegment(sketch, "E2.2.22.0", {"start": v(-8.25, -20.85) * mm, "end": v(-8.25, -22.85) * mm});
            skLineSegment(sketch, "E2.2.22.1", {"start": v(-8.25, -22.85) * mm, "end": v(8.25, -22.85) * mm});
            skLineSegment(sketch, "E2.2.22.2", {"start": v(-8.25, -20.85) * mm, "end": v(8.25, -20.85) * mm});
            skLineSegment(sketch, "E2.2.22.3", {"start": v(8.25, -20.85) * mm, "end": v(8.25, -22.85) * mm});
            skLineSegment(sketch, "E2.2.23.0", {"start": v(-8.25, -23.15) * mm, "end": v(-8.25, -25.15) * mm});
            skLineSegment(sketch, "E2.2.23.1", {"start": v(-8.25, -25.15) * mm, "end": v(8.25, -25.15) * mm});
            skLineSegment(sketch, "E2.2.23.2", {"start": v(-8.25, -23.15) * mm, "end": v(8.25, -23.15) * mm});
            skLineSegment(sketch, "E2.2.23.3", {"start": v(8.25, -23.15) * mm, "end": v(8.25, -25.15) * mm});
            skLineSegment(sketch, "E2.2.24.0", {"start": v(-8.25, -25.45) * mm, "end": v(-8.25, -27.45) * mm});
            skLineSegment(sketch, "E2.2.24.1", {"start": v(-8.25, -27.45) * mm, "end": v(8.25, -27.45) * mm});
            skLineSegment(sketch, "E2.2.24.2", {"start": v(-8.25, -25.45) * mm, "end": v(8.25, -25.45) * mm});
            skLineSegment(sketch, "E2.2.24.3", {"start": v(8.25, -25.45) * mm, "end": v(8.25, -27.45) * mm});
            skLineSegment(sketch, "E2.2.25.0", {"start": v(-8.25, -27.75) * mm, "end": v(-8.25, -29.75) * mm});
            skLineSegment(sketch, "E2.2.25.1", {"start": v(-8.25, -29.75) * mm, "end": v(8.25, -29.75) * mm});
            skLineSegment(sketch, "E2.2.25.2", {"start": v(-8.25, -27.75) * mm, "end": v(8.25, -27.75) * mm});
            skLineSegment(sketch, "E2.2.25.3", {"start": v(8.25, -27.75) * mm, "end": v(8.25, -29.75) * mm});
            skLineSegment(sketch, "E2.3.0.0", {"start": v(8.55, 29.75) * mm, "end": v(8.55, 27.75) * mm});
            skLineSegment(sketch, "E2.3.0.1", {"start": v(8.55, 27.75) * mm, "end": v(25.05, 27.75) * mm});
            skLineSegment(sketch, "E2.3.0.2", {"start": v(8.55, 29.75) * mm, "end": v(25.05, 29.75) * mm});
            skLineSegment(sketch, "E2.3.0.3", {"start": v(25.05, 29.75) * mm, "end": v(25.05, 27.75) * mm});
            skLineSegment(sketch, "E2.3.1.0", {"start": v(8.55, 27.45) * mm, "end": v(8.55, 25.45) * mm});
            skLineSegment(sketch, "E2.3.1.1", {"start": v(8.55, 25.45) * mm, "end": v(25.05, 25.45) * mm});
            skLineSegment(sketch, "E2.3.1.2", {"start": v(8.55, 27.45) * mm, "end": v(25.05, 27.45) * mm});
            skLineSegment(sketch, "E2.3.1.3", {"start": v(25.05, 27.45) * mm, "end": v(25.05, 25.45) * mm});
            skLineSegment(sketch, "E2.3.2.0", {"start": v(8.55, 25.15) * mm, "end": v(8.55, 23.15) * mm});
            skLineSegment(sketch, "E2.3.2.1", {"start": v(8.55, 23.15) * mm, "end": v(25.05, 23.15) * mm});
            skLineSegment(sketch, "E2.3.2.2", {"start": v(8.55, 25.15) * mm, "end": v(25.05, 25.15) * mm});
            skLineSegment(sketch, "E2.3.2.3", {"start": v(25.05, 25.15) * mm, "end": v(25.05, 23.15) * mm});
            skLineSegment(sketch, "E2.3.3.0", {"start": v(8.55, 22.85) * mm, "end": v(8.55, 20.85) * mm});
            skLineSegment(sketch, "E2.3.3.1", {"start": v(8.55, 20.85) * mm, "end": v(25.05, 20.85) * mm});
            skLineSegment(sketch, "E2.3.3.2", {"start": v(8.55, 22.85) * mm, "end": v(25.05, 22.85) * mm});
            skLineSegment(sketch, "E2.3.3.3", {"start": v(25.05, 22.85) * mm, "end": v(25.05, 20.85) * mm});
            skLineSegment(sketch, "E2.3.4.0", {"start": v(8.55, 20.55) * mm, "end": v(8.55, 18.55) * mm});
            skLineSegment(sketch, "E2.3.4.1", {"start": v(8.55, 18.55) * mm, "end": v(25.05, 18.55) * mm});
            skLineSegment(sketch, "E2.3.4.2", {"start": v(8.55, 20.55) * mm, "end": v(25.05, 20.55) * mm});
            skLineSegment(sketch, "E2.3.4.3", {"start": v(25.05, 20.55) * mm, "end": v(25.05, 18.55) * mm});
            skLineSegment(sketch, "E2.3.5.0", {"start": v(8.55, 18.25) * mm, "end": v(8.55, 16.25) * mm});
            skLineSegment(sketch, "E2.3.5.1", {"start": v(8.55, 16.25) * mm, "end": v(25.05, 16.25) * mm});
            skLineSegment(sketch, "E2.3.5.2", {"start": v(8.55, 18.25) * mm, "end": v(25.05, 18.25) * mm});
            skLineSegment(sketch, "E2.3.5.3", {"start": v(25.05, 18.25) * mm, "end": v(25.05, 16.25) * mm});
            skLineSegment(sketch, "E2.3.6.0", {"start": v(8.55, 15.95) * mm, "end": v(8.55, 13.95) * mm});
            skLineSegment(sketch, "E2.3.6.1", {"start": v(8.55, 13.95) * mm, "end": v(25.05, 13.95) * mm});
            skLineSegment(sketch, "E2.3.6.2", {"start": v(8.55, 15.95) * mm, "end": v(25.05, 15.95) * mm});
            skLineSegment(sketch, "E2.3.6.3", {"start": v(25.05, 15.95) * mm, "end": v(25.05, 13.95) * mm});
            skLineSegment(sketch, "E2.3.7.0", {"start": v(8.55, 13.65) * mm, "end": v(8.55, 11.65) * mm});
            skLineSegment(sketch, "E2.3.7.1", {"start": v(8.55, 11.65) * mm, "end": v(25.05, 11.65) * mm});
            skLineSegment(sketch, "E2.3.7.2", {"start": v(8.55, 13.65) * mm, "end": v(25.05, 13.65) * mm});
            skLineSegment(sketch, "E2.3.7.3", {"start": v(25.05, 13.65) * mm, "end": v(25.05, 11.65) * mm});
            skLineSegment(sketch, "E2.3.8.0", {"start": v(8.55, 11.35) * mm, "end": v(8.55, 9.35) * mm});
            skLineSegment(sketch, "E2.3.8.1", {"start": v(8.55, 9.35) * mm, "end": v(25.05, 9.35) * mm});
            skLineSegment(sketch, "E2.3.8.2", {"start": v(8.55, 11.35) * mm, "end": v(25.05, 11.35) * mm});
            skLineSegment(sketch, "E2.3.8.3", {"start": v(25.05, 11.35) * mm, "end": v(25.05, 9.35) * mm});
            skLineSegment(sketch, "E2.3.9.0", {"start": v(8.55, 9.05) * mm, "end": v(8.55, 7.05) * mm});
            skLineSegment(sketch, "E2.3.9.1", {"start": v(8.55, 7.05) * mm, "end": v(25.05, 7.05) * mm});
            skLineSegment(sketch, "E2.3.9.2", {"start": v(8.55, 9.05) * mm, "end": v(25.05, 9.05) * mm});
            skLineSegment(sketch, "E2.3.9.3", {"start": v(25.05, 9.05) * mm, "end": v(25.05, 7.05) * mm});
            skLineSegment(sketch, "E2.3.10.0", {"start": v(8.55, 6.75) * mm, "end": v(8.55, 4.75) * mm});
            skLineSegment(sketch, "E2.3.10.1", {"start": v(8.55, 4.75) * mm, "end": v(25.05, 4.75) * mm});
            skLineSegment(sketch, "E2.3.10.2", {"start": v(8.55, 6.75) * mm, "end": v(25.05, 6.75) * mm});
            skLineSegment(sketch, "E2.3.10.3", {"start": v(25.05, 6.75) * mm, "end": v(25.05, 4.75) * mm});
            skLineSegment(sketch, "E2.3.11.0", {"start": v(8.55, 4.45) * mm, "end": v(8.55, 2.45) * mm});
            skLineSegment(sketch, "E2.3.11.1", {"start": v(8.55, 2.45) * mm, "end": v(25.05, 2.45) * mm});
            skLineSegment(sketch, "E2.3.11.2", {"start": v(8.55, 4.45) * mm, "end": v(25.05, 4.45) * mm});
            skLineSegment(sketch, "E2.3.11.3", {"start": v(25.05, 4.45) * mm, "end": v(25.05, 2.45) * mm});
            skLineSegment(sketch, "E2.3.12.0", {"start": v(8.55, 2.15) * mm, "end": v(8.55, 0.15) * mm});
            skLineSegment(sketch, "E2.3.12.1", {"start": v(8.55, 0.15) * mm, "end": v(25.05, 0.15) * mm});
            skLineSegment(sketch, "E2.3.12.2", {"start": v(8.55, 2.15) * mm, "end": v(25.05, 2.15) * mm});
            skLineSegment(sketch, "E2.3.12.3", {"start": v(25.05, 2.15) * mm, "end": v(25.05, 0.15) * mm});
            skLineSegment(sketch, "E2.3.13.0", {"start": v(8.55, -0.15) * mm, "end": v(8.55, -2.15) * mm});
            skLineSegment(sketch, "E2.3.13.1", {"start": v(8.55, -2.15) * mm, "end": v(25.05, -2.15) * mm});
            skLineSegment(sketch, "E2.3.13.2", {"start": v(8.55, -0.15) * mm, "end": v(25.05, -0.15) * mm});
            skLineSegment(sketch, "E2.3.13.3", {"start": v(25.05, -0.15) * mm, "end": v(25.05, -2.15) * mm});
            skLineSegment(sketch, "E2.3.14.0", {"start": v(8.55, -2.45) * mm, "end": v(8.55, -4.45) * mm});
            skLineSegment(sketch, "E2.3.14.1", {"start": v(8.55, -4.45) * mm, "end": v(25.05, -4.45) * mm});
            skLineSegment(sketch, "E2.3.14.2", {"start": v(8.55, -2.45) * mm, "end": v(25.05, -2.45) * mm});
            skLineSegment(sketch, "E2.3.14.3", {"start": v(25.05, -2.45) * mm, "end": v(25.05, -4.45) * mm});
            skLineSegment(sketch, "E2.3.15.0", {"start": v(8.55, -4.75) * mm, "end": v(8.55, -6.75) * mm});
            skLineSegment(sketch, "E2.3.15.1", {"start": v(8.55, -6.75) * mm, "end": v(25.05, -6.75) * mm});
            skLineSegment(sketch, "E2.3.15.2", {"start": v(8.55, -4.75) * mm, "end": v(25.05, -4.75) * mm});
            skLineSegment(sketch, "E2.3.15.3", {"start": v(25.05, -4.75) * mm, "end": v(25.05, -6.75) * mm});
            skLineSegment(sketch, "E2.3.16.0", {"start": v(8.55, -7.05) * mm, "end": v(8.55, -9.05) * mm});
            skLineSegment(sketch, "E2.3.16.1", {"start": v(8.55, -9.05) * mm, "end": v(25.05, -9.05) * mm});
            skLineSegment(sketch, "E2.3.16.2", {"start": v(8.55, -7.05) * mm, "end": v(25.05, -7.05) * mm});
            skLineSegment(sketch, "E2.3.16.3", {"start": v(25.05, -7.05) * mm, "end": v(25.05, -9.05) * mm});
            skLineSegment(sketch, "E2.3.17.0", {"start": v(8.55, -9.35) * mm, "end": v(8.55, -11.35) * mm});
            skLineSegment(sketch, "E2.3.17.1", {"start": v(8.55, -11.35) * mm, "end": v(25.05, -11.35) * mm});
            skLineSegment(sketch, "E2.3.17.2", {"start": v(8.55, -9.35) * mm, "end": v(25.05, -9.35) * mm});
            skLineSegment(sketch, "E2.3.17.3", {"start": v(25.05, -9.35) * mm, "end": v(25.05, -11.35) * mm});
            skLineSegment(sketch, "E2.3.18.0", {"start": v(8.55, -11.65) * mm, "end": v(8.55, -13.65) * mm});
            skLineSegment(sketch, "E2.3.18.1", {"start": v(8.55, -13.65) * mm, "end": v(25.05, -13.65) * mm});
            skLineSegment(sketch, "E2.3.18.2", {"start": v(8.55, -11.65) * mm, "end": v(25.05, -11.65) * mm});
            skLineSegment(sketch, "E2.3.18.3", {"start": v(25.05, -11.65) * mm, "end": v(25.05, -13.65) * mm});
            skLineSegment(sketch, "E2.3.19.0", {"start": v(8.55, -13.95) * mm, "end": v(8.55, -15.95) * mm});
            skLineSegment(sketch, "E2.3.19.1", {"start": v(8.55, -15.95) * mm, "end": v(25.05, -15.95) * mm});
            skLineSegment(sketch, "E2.3.19.2", {"start": v(8.55, -13.95) * mm, "end": v(25.05, -13.95) * mm});
            skLineSegment(sketch, "E2.3.19.3", {"start": v(25.05, -13.95) * mm, "end": v(25.05, -15.95) * mm});
            skLineSegment(sketch, "E2.3.20.0", {"start": v(8.55, -16.25) * mm, "end": v(8.55, -18.25) * mm});
            skLineSegment(sketch, "E2.3.20.1", {"start": v(8.55, -18.25) * mm, "end": v(25.05, -18.25) * mm});
            skLineSegment(sketch, "E2.3.20.2", {"start": v(8.55, -16.25) * mm, "end": v(25.05, -16.25) * mm});
            skLineSegment(sketch, "E2.3.20.3", {"start": v(25.05, -16.25) * mm, "end": v(25.05, -18.25) * mm});
            skLineSegment(sketch, "E2.3.21.0", {"start": v(8.55, -18.55) * mm, "end": v(8.55, -20.55) * mm});
            skLineSegment(sketch, "E2.3.21.1", {"start": v(8.55, -20.55) * mm, "end": v(25.05, -20.55) * mm});
            skLineSegment(sketch, "E2.3.21.2", {"start": v(8.55, -18.55) * mm, "end": v(25.05, -18.55) * mm});
            skLineSegment(sketch, "E2.3.21.3", {"start": v(25.05, -18.55) * mm, "end": v(25.05, -20.55) * mm});
            skLineSegment(sketch, "E2.3.22.0", {"start": v(8.55, -20.85) * mm, "end": v(8.55, -22.85) * mm});
            skLineSegment(sketch, "E2.3.22.1", {"start": v(8.55, -22.85) * mm, "end": v(25.05, -22.85) * mm});
            skLineSegment(sketch, "E2.3.22.2", {"start": v(8.55, -20.85) * mm, "end": v(25.05, -20.85) * mm});
            skLineSegment(sketch, "E2.3.22.3", {"start": v(25.05, -20.85) * mm, "end": v(25.05, -22.85) * mm});
            skLineSegment(sketch, "E2.3.23.0", {"start": v(8.55, -23.15) * mm, "end": v(8.55, -25.15) * mm});
            skLineSegment(sketch, "E2.3.23.1", {"start": v(8.55, -25.15) * mm, "end": v(25.05, -25.15) * mm});
            skLineSegment(sketch, "E2.3.23.2", {"start": v(8.55, -23.15) * mm, "end": v(25.05, -23.15) * mm});
            skLineSegment(sketch, "E2.3.23.3", {"start": v(25.05, -23.15) * mm, "end": v(25.05, -25.15) * mm});
            skLineSegment(sketch, "E2.3.24.0", {"start": v(8.55, -25.45) * mm, "end": v(8.55, -27.45) * mm});
            skLineSegment(sketch, "E2.3.24.1", {"start": v(8.55, -27.45) * mm, "end": v(25.05, -27.45) * mm});
            skLineSegment(sketch, "E2.3.24.2", {"start": v(8.55, -25.45) * mm, "end": v(25.05, -25.45) * mm});
            skLineSegment(sketch, "E2.3.24.3", {"start": v(25.05, -25.45) * mm, "end": v(25.05, -27.45) * mm});
            skLineSegment(sketch, "E2.3.25.0", {"start": v(8.55, -27.75) * mm, "end": v(8.55, -29.75) * mm});
            skLineSegment(sketch, "E2.3.25.1", {"start": v(8.55, -29.75) * mm, "end": v(25.05, -29.75) * mm});
            skLineSegment(sketch, "E2.3.25.2", {"start": v(8.55, -27.75) * mm, "end": v(25.05, -27.75) * mm});
            skLineSegment(sketch, "E2.3.25.3", {"start": v(25.05, -27.75) * mm, "end": v(25.05, -29.75) * mm});
            skLineSegment(sketch, "E2.4.0.0", {"start": v(25.35, 29.75) * mm, "end": v(25.35, 27.75) * mm});
            skLineSegment(sketch, "E2.4.0.1", {"start": v(25.35, 27.75) * mm, "end": v(41.85, 27.75) * mm});
            skLineSegment(sketch, "E2.4.0.2", {"start": v(25.35, 29.75) * mm, "end": v(41.85, 29.75) * mm});
            skLineSegment(sketch, "E2.4.0.3", {"start": v(41.85, 29.75) * mm, "end": v(41.85, 27.75) * mm});
            skLineSegment(sketch, "E2.4.1.0", {"start": v(25.35, 27.45) * mm, "end": v(25.35, 25.45) * mm});
            skLineSegment(sketch, "E2.4.1.1", {"start": v(25.35, 25.45) * mm, "end": v(41.85, 25.45) * mm});
            skLineSegment(sketch, "E2.4.1.2", {"start": v(25.35, 27.45) * mm, "end": v(41.85, 27.45) * mm});
            skLineSegment(sketch, "E2.4.1.3", {"start": v(41.85, 27.45) * mm, "end": v(41.85, 25.45) * mm});
            skLineSegment(sketch, "E2.4.2.0", {"start": v(25.35, 25.15) * mm, "end": v(25.35, 23.15) * mm});
            skLineSegment(sketch, "E2.4.2.1", {"start": v(25.35, 23.15) * mm, "end": v(41.85, 23.15) * mm});
            skLineSegment(sketch, "E2.4.2.2", {"start": v(25.35, 25.15) * mm, "end": v(41.85, 25.15) * mm});
            skLineSegment(sketch, "E2.4.2.3", {"start": v(41.85, 25.15) * mm, "end": v(41.85, 23.15) * mm});
            skLineSegment(sketch, "E2.4.3.0", {"start": v(25.35, 22.85) * mm, "end": v(25.35, 20.85) * mm});
            skLineSegment(sketch, "E2.4.3.1", {"start": v(25.35, 20.85) * mm, "end": v(41.85, 20.85) * mm});
            skLineSegment(sketch, "E2.4.3.2", {"start": v(25.35, 22.85) * mm, "end": v(41.85, 22.85) * mm});
            skLineSegment(sketch, "E2.4.3.3", {"start": v(41.85, 22.85) * mm, "end": v(41.85, 20.85) * mm});
            skLineSegment(sketch, "E2.4.4.0", {"start": v(25.35, 20.55) * mm, "end": v(25.35, 18.55) * mm});
            skLineSegment(sketch, "E2.4.4.1", {"start": v(25.35, 18.55) * mm, "end": v(41.85, 18.55) * mm});
            skLineSegment(sketch, "E2.4.4.2", {"start": v(25.35, 20.55) * mm, "end": v(41.85, 20.55) * mm});
            skLineSegment(sketch, "E2.4.4.3", {"start": v(41.85, 20.55) * mm, "end": v(41.85, 18.55) * mm});
            skLineSegment(sketch, "E2.4.5.0", {"start": v(25.35, 18.25) * mm, "end": v(25.35, 16.25) * mm});
            skLineSegment(sketch, "E2.4.5.1", {"start": v(25.35, 16.25) * mm, "end": v(41.85, 16.25) * mm});
            skLineSegment(sketch, "E2.4.5.2", {"start": v(25.35, 18.25) * mm, "end": v(41.85, 18.25) * mm});
            skLineSegment(sketch, "E2.4.5.3", {"start": v(41.85, 18.25) * mm, "end": v(41.85, 16.25) * mm});
            skLineSegment(sketch, "E2.4.6.0", {"start": v(25.35, 15.95) * mm, "end": v(25.35, 13.95) * mm});
            skLineSegment(sketch, "E2.4.6.1", {"start": v(25.35, 13.95) * mm, "end": v(41.85, 13.95) * mm});
            skLineSegment(sketch, "E2.4.6.2", {"start": v(25.35, 15.95) * mm, "end": v(41.85, 15.95) * mm});
            skLineSegment(sketch, "E2.4.6.3", {"start": v(41.85, 15.95) * mm, "end": v(41.85, 13.95) * mm});
            skLineSegment(sketch, "E2.4.7.0", {"start": v(25.35, 13.65) * mm, "end": v(25.35, 11.65) * mm});
            skLineSegment(sketch, "E2.4.7.1", {"start": v(25.35, 11.65) * mm, "end": v(41.85, 11.65) * mm});
            skLineSegment(sketch, "E2.4.7.2", {"start": v(25.35, 13.65) * mm, "end": v(41.85, 13.65) * mm});
            skLineSegment(sketch, "E2.4.7.3", {"start": v(41.85, 13.65) * mm, "end": v(41.85, 11.65) * mm});
            skLineSegment(sketch, "E2.4.8.0", {"start": v(25.35, 11.35) * mm, "end": v(25.35, 9.35) * mm});
            skLineSegment(sketch, "E2.4.8.1", {"start": v(25.35, 9.35) * mm, "end": v(41.85, 9.35) * mm});
            skLineSegment(sketch, "E2.4.8.2", {"start": v(25.35, 11.35) * mm, "end": v(41.85, 11.35) * mm});
            skLineSegment(sketch, "E2.4.8.3", {"start": v(41.85, 11.35) * mm, "end": v(41.85, 9.35) * mm});
            skLineSegment(sketch, "E2.4.9.0", {"start": v(25.35, 9.05) * mm, "end": v(25.35, 7.05) * mm});
            skLineSegment(sketch, "E2.4.9.1", {"start": v(25.35, 7.05) * mm, "end": v(41.85, 7.05) * mm});
            skLineSegment(sketch, "E2.4.9.2", {"start": v(25.35, 9.05) * mm, "end": v(41.85, 9.05) * mm});
            skLineSegment(sketch, "E2.4.9.3", {"start": v(41.85, 9.05) * mm, "end": v(41.85, 7.05) * mm});
            skLineSegment(sketch, "E2.4.10.0", {"start": v(25.35, 6.75) * mm, "end": v(25.35, 4.75) * mm});
            skLineSegment(sketch, "E2.4.10.1", {"start": v(25.35, 4.75) * mm, "end": v(41.85, 4.75) * mm});
            skLineSegment(sketch, "E2.4.10.2", {"start": v(25.35, 6.75) * mm, "end": v(41.85, 6.75) * mm});
            skLineSegment(sketch, "E2.4.10.3", {"start": v(41.85, 6.75) * mm, "end": v(41.85, 4.75) * mm});
            skLineSegment(sketch, "E2.4.11.0", {"start": v(25.35, 4.45) * mm, "end": v(25.35, 2.45) * mm});
            skLineSegment(sketch, "E2.4.11.1", {"start": v(25.35, 2.45) * mm, "end": v(41.85, 2.45) * mm});
            skLineSegment(sketch, "E2.4.11.2", {"start": v(25.35, 4.45) * mm, "end": v(41.85, 4.45) * mm});
            skLineSegment(sketch, "E2.4.11.3", {"start": v(41.85, 4.45) * mm, "end": v(41.85, 2.45) * mm});
            skLineSegment(sketch, "E2.4.12.0", {"start": v(25.35, 2.15) * mm, "end": v(25.35, 0.15) * mm});
            skLineSegment(sketch, "E2.4.12.1", {"start": v(25.35, 0.15) * mm, "end": v(41.85, 0.15) * mm});
            skLineSegment(sketch, "E2.4.12.2", {"start": v(25.35, 2.15) * mm, "end": v(41.85, 2.15) * mm});
            skLineSegment(sketch, "E2.4.12.3", {"start": v(41.85, 2.15) * mm, "end": v(41.85, 0.15) * mm});
            skLineSegment(sketch, "E2.4.13.0", {"start": v(25.35, -0.15) * mm, "end": v(25.35, -2.15) * mm});
            skLineSegment(sketch, "E2.4.13.1", {"start": v(25.35, -2.15) * mm, "end": v(41.85, -2.15) * mm});
            skLineSegment(sketch, "E2.4.13.2", {"start": v(25.35, -0.15) * mm, "end": v(41.85, -0.15) * mm});
            skLineSegment(sketch, "E2.4.13.3", {"start": v(41.85, -0.15) * mm, "end": v(41.85, -2.15) * mm});
            skLineSegment(sketch, "E2.4.14.0", {"start": v(25.35, -2.45) * mm, "end": v(25.35, -4.45) * mm});
            skLineSegment(sketch, "E2.4.14.1", {"start": v(25.35, -4.45) * mm, "end": v(41.85, -4.45) * mm});
            skLineSegment(sketch, "E2.4.14.2", {"start": v(25.35, -2.45) * mm, "end": v(41.85, -2.45) * mm});
            skLineSegment(sketch, "E2.4.14.3", {"start": v(41.85, -2.45) * mm, "end": v(41.85, -4.45) * mm});
            skLineSegment(sketch, "E2.4.15.0", {"start": v(25.35, -4.75) * mm, "end": v(25.35, -6.75) * mm});
            skLineSegment(sketch, "E2.4.15.1", {"start": v(25.35, -6.75) * mm, "end": v(41.85, -6.75) * mm});
            skLineSegment(sketch, "E2.4.15.2", {"start": v(25.35, -4.75) * mm, "end": v(41.85, -4.75) * mm});
            skLineSegment(sketch, "E2.4.15.3", {"start": v(41.85, -4.75) * mm, "end": v(41.85, -6.75) * mm});
            skLineSegment(sketch, "E2.4.16.0", {"start": v(25.35, -7.05) * mm, "end": v(25.35, -9.05) * mm});
            skLineSegment(sketch, "E2.4.16.1", {"start": v(25.35, -9.05) * mm, "end": v(41.85, -9.05) * mm});
            skLineSegment(sketch, "E2.4.16.2", {"start": v(25.35, -7.05) * mm, "end": v(41.85, -7.05) * mm});
            skLineSegment(sketch, "E2.4.16.3", {"start": v(41.85, -7.05) * mm, "end": v(41.85, -9.05) * mm});
            skLineSegment(sketch, "E2.4.17.0", {"start": v(25.35, -9.35) * mm, "end": v(25.35, -11.35) * mm});
            skLineSegment(sketch, "E2.4.17.1", {"start": v(25.35, -11.35) * mm, "end": v(41.85, -11.35) * mm});
            skLineSegment(sketch, "E2.4.17.2", {"start": v(25.35, -9.35) * mm, "end": v(41.85, -9.35) * mm});
            skLineSegment(sketch, "E2.4.17.3", {"start": v(41.85, -9.35) * mm, "end": v(41.85, -11.35) * mm});
            skLineSegment(sketch, "E2.4.18.0", {"start": v(25.35, -11.65) * mm, "end": v(25.35, -13.65) * mm});
            skLineSegment(sketch, "E2.4.18.1", {"start": v(25.35, -13.65) * mm, "end": v(41.85, -13.65) * mm});
            skLineSegment(sketch, "E2.4.18.2", {"start": v(25.35, -11.65) * mm, "end": v(41.85, -11.65) * mm});
            skLineSegment(sketch, "E2.4.18.3", {"start": v(41.85, -11.65) * mm, "end": v(41.85, -13.65) * mm});
            skLineSegment(sketch, "E2.4.19.0", {"start": v(25.35, -13.95) * mm, "end": v(25.35, -15.95) * mm});
            skLineSegment(sketch, "E2.4.19.1", {"start": v(25.35, -15.95) * mm, "end": v(41.85, -15.95) * mm});
            skLineSegment(sketch, "E2.4.19.2", {"start": v(25.35, -13.95) * mm, "end": v(41.85, -13.95) * mm});
            skLineSegment(sketch, "E2.4.19.3", {"start": v(41.85, -13.95) * mm, "end": v(41.85, -15.95) * mm});
            skLineSegment(sketch, "E2.4.20.0", {"start": v(25.35, -16.25) * mm, "end": v(25.35, -18.25) * mm});
            skLineSegment(sketch, "E2.4.20.1", {"start": v(25.35, -18.25) * mm, "end": v(41.85, -18.25) * mm});
            skLineSegment(sketch, "E2.4.20.2", {"start": v(25.35, -16.25) * mm, "end": v(41.85, -16.25) * mm});
            skLineSegment(sketch, "E2.4.20.3", {"start": v(41.85, -16.25) * mm, "end": v(41.85, -18.25) * mm});
            skLineSegment(sketch, "E2.4.21.0", {"start": v(25.35, -18.55) * mm, "end": v(25.35, -20.55) * mm});
            skLineSegment(sketch, "E2.4.21.1", {"start": v(25.35, -20.55) * mm, "end": v(41.85, -20.55) * mm});
            skLineSegment(sketch, "E2.4.21.2", {"start": v(25.35, -18.55) * mm, "end": v(41.85, -18.55) * mm});
            skLineSegment(sketch, "E2.4.21.3", {"start": v(41.85, -18.55) * mm, "end": v(41.85, -20.55) * mm});
            skLineSegment(sketch, "E2.4.22.0", {"start": v(25.35, -20.85) * mm, "end": v(25.35, -22.85) * mm});
            skLineSegment(sketch, "E2.4.22.1", {"start": v(25.35, -22.85) * mm, "end": v(41.85, -22.85) * mm});
            skLineSegment(sketch, "E2.4.22.2", {"start": v(25.35, -20.85) * mm, "end": v(41.85, -20.85) * mm});
            skLineSegment(sketch, "E2.4.22.3", {"start": v(41.85, -20.85) * mm, "end": v(41.85, -22.85) * mm});
            skLineSegment(sketch, "E2.4.23.0", {"start": v(25.35, -23.15) * mm, "end": v(25.35, -25.15) * mm});
            skLineSegment(sketch, "E2.4.23.1", {"start": v(25.35, -25.15) * mm, "end": v(41.85, -25.15) * mm});
            skLineSegment(sketch, "E2.4.23.2", {"start": v(25.35, -23.15) * mm, "end": v(41.85, -23.15) * mm});
            skLineSegment(sketch, "E2.4.23.3", {"start": v(41.85, -23.15) * mm, "end": v(41.85, -25.15) * mm});
            skLineSegment(sketch, "E2.4.24.0", {"start": v(25.35, -25.45) * mm, "end": v(25.35, -27.45) * mm});
            skLineSegment(sketch, "E2.4.24.1", {"start": v(25.35, -27.45) * mm, "end": v(41.85, -27.45) * mm});
            skLineSegment(sketch, "E2.4.24.2", {"start": v(25.35, -25.45) * mm, "end": v(41.85, -25.45) * mm});
            skLineSegment(sketch, "E2.4.24.3", {"start": v(41.85, -25.45) * mm, "end": v(41.85, -27.45) * mm});
            skLineSegment(sketch, "E2.4.25.0", {"start": v(25.35, -27.75) * mm, "end": v(25.35, -29.75) * mm});
            skLineSegment(sketch, "E2.4.25.1", {"start": v(25.35, -29.75) * mm, "end": v(41.85, -29.75) * mm});
            skLineSegment(sketch, "E2.4.25.2", {"start": v(25.35, -27.75) * mm, "end": v(41.85, -27.75) * mm});
            skLineSegment(sketch, "E2.4.25.3", {"start": v(41.85, -27.75) * mm, "end": v(41.85, -29.75) * mm});
            skLineSegment(sketch, "E2.direction1", {"start": v(-41.85, 27.75) * mm, "end": v(-25.05, 27.75) * mm, "construction": true});
            skLineSegment(sketch, "E2.direction2", {"start": v(-41.85, 27.75) * mm, "end": v(-41.85, 25.45) * mm, "construction": true});
            skLineSegment(sketch, "E3", {"start": v(-42.56, 30.46) * mm, "end": v(-41.85, 29.75) * mm, "construction": true});
            skLineSegment(sketch, "E4", {"start": v(42.56, -30.46) * mm, "end": v(41.85, -29.75) * mm, "construction": true});
            skSolve(sketch);
        }
        {
            var Q0;
            Q0 = qSketchRegion(id + "F0", true);
            extrude(context, id + "F1", {"entities" : qUnion([Q0]), "depth" : 18 * mm});
        }
        {
            var Q0;
            Q0=qCreatedBy(makeId("Top.planeOp"),FACE);
            var sketch = newSketch(context, id + "F2", { "sketchPlane" : qUnion([Q0])});
            skLineSegment(sketch, "E5.0", {"start": v(42.56, -30.46) * mm, "end": v(-42.56, -30.46) * mm});
            skLineSegment(sketch, "E6.0", {"start": v(-42.56, -30.46) * mm, "end": v(-42.56, 30.46) * mm});
            skLineSegment(sketch, "E7.0", {"start": v(42.56, -30.46) * mm, "end": v(42.56, 30.46) * mm});
            skLineSegment(sketch, "E8.0", {"start": v(42.56, 30.46) * mm, "end": v(-42.56, 30.46) * mm});
            skSolve(sketch);
        }
        {
            var Q0;
            Q0 = qSketchRegion(id + "F2", true);
            extrude(context, id + "F3", {"entities" : qUnion([Q0]), "operationType" : NewBodyOperationType.ADD, "depth" : 1 * mm});
        }
        {
            var Q0;
            Q0=qCreatedBy(makeId("Front.planeOp"),FACE);
            var sketch = newSketch(context, id + "F4", { "sketchPlane" : qUnion([Q0])});
            skLineSegment(sketch, "E9", {"start": v(0, 0) * mm, "end": v(0, 20) * mm, "construction": true});
            skSolve(sketch);
        }
        {
            var Q0;
            Q0=makeQuery(id+"F1.opExtrude","SWEPT_BODY",BODY,{"disambiguationData":[OSD([sQuery(id+"F0.wireOp",EDGE,"E0.bottom"),sQuery(id+"F0.wireOp",EDGE,"E0.top"),sQuery(id+"F0.wireOp",EDGE,"E0.left"),sQuery(id+"F0.wireOp",EDGE,"E0.right"),sQuery(id+"F0.wireOp",EDGE,"E1.bottom"),sQuery(id+"F0.wireOp",EDGE,"E1.top"),sQuery(id+"F0.wireOp",EDGE,"E1.left"),sQuery(id+"F0.wireOp",EDGE,"E1.right"),sQuery(id+"F0.wireOp",EDGE,"E2.0.1.0"),sQuery(id+"F0.wireOp",EDGE,"E2.0.1.1"),sQuery(id+"F0.wireOp",EDGE,"E2.0.1.2"),sQuery(id+"F0.wireOp",EDGE,"E2.0.1.3"),sQuery(id+"F0.wireOp",EDGE,"E2.0.2.0"),sQuery(id+"F0.wireOp",EDGE,"E2.0.2.1"),sQuery(id+"F0.wireOp",EDGE,"E2.0.2.2"),sQuery(id+"F0.wireOp",EDGE,"E2.0.2.3"),sQuery(id+"F0.wireOp",EDGE,"E2.0.3.0"),sQuery(id+"F0.wireOp",EDGE,"E2.0.3.1"),sQuery(id+"F0.wireOp",EDGE,"E2.0.3.2"),sQuery(id+"F0.wireOp",EDGE,"E2.0.3.3"),sQuery(id+"F0.wireOp",EDGE,"E2.0.4.0"),sQuery(id+"F0.wireOp",EDGE,"E2.0.4.1"),sQuery(id+"F0.wireOp",EDGE,"E2.0.4.2"),sQuery(id+"F0.wireOp",EDGE,"E2.0.4.3"),sQuery(id+"F0.wireOp",EDGE,"E2.0.5.0"),sQuery(id+"F0.wireOp",EDGE,"E2.0.5.1"),sQuery(id+"F0.wireOp",EDGE,"E2.0.5.2"),sQuery(id+"F0.wireOp",EDGE,"E2.0.5.3"),sQuery(id+"F0.wireOp",EDGE,"E2.0.6.0"),sQuery(id+"F0.wireOp",EDGE,"E2.0.6.1"),sQuery(id+"F0.wireOp",EDGE,"E2.0.6.2"),sQuery(id+"F0.wireOp",EDGE,"E2.0.6.3"),sQuery(id+"F0.wireOp",EDGE,"E2.0.7.0"),sQuery(id+"F0.wireOp",EDGE,"E2.0.7.1"),sQuery(id+"F0.wireOp",EDGE,"E2.0.7.2"),sQuery(id+"F0.wireOp",EDGE,"E2.0.7.3"),sQuery(id+"F0.wireOp",EDGE,"E2.0.8.0"),sQuery(id+"F0.wireOp",EDGE,"E2.0.8.1"),sQuery(id+"F0.wireOp",EDGE,"E2.0.8.2"),sQuery(id+"F0.wireOp",EDGE,"E2.0.8.3"),sQuery(id+"F0.wireOp",EDGE,"E2.0.9.0"),sQuery(id+"F0.wireOp",EDGE,"E2.0.9.1"),sQuery(id+"F0.wireOp",EDGE,"E2.0.9.2"),sQuery(id+"F0.wireOp",EDGE,"E2.0.9.3"),sQuery(id+"F0.wireOp",EDGE,"E2.0.10.0"),sQuery(id+"F0.wireOp",EDGE,"E2.0.10.1"),sQuery(id+"F0.wireOp",EDGE,"E2.0.10.2"),sQuery(id+"F0.wireOp",EDGE,"E2.0.10.3"),sQuery(id+"F0.wireOp",EDGE,"E2.0.11.0"),sQuery(id+"F0.wireOp",EDGE,"E2.0.11.1"),sQuery(id+"F0.wireOp",EDGE,"E2.0.11.2"),sQuery(id+"F0.wireOp",EDGE,"E2.0.11.3"),sQuery(id+"F0.wireOp",EDGE,"E2.0.12.0"),sQuery(id+"F0.wireOp",EDGE,"E2.0.12.1"),sQuery(id+"F0.wireOp",EDGE,"E2.0.12.2"),sQuery(id+"F0.wireOp",EDGE,"E2.0.12.3"),sQuery(id+"F0.wireOp",EDGE,"E2.0.13.0"),sQuery(id+"F0.wireOp",EDGE,"E2.0.13.1"),sQuery(id+"F0.wireOp",EDGE,"E2.0.13.2"),sQuery(id+"F0.wireOp",EDGE,"E2.0.13.3"),sQuery(id+"F0.wireOp",EDGE,"E2.0.14.0"),sQuery(id+"F0.wireOp",EDGE,"E2.0.14.1"),sQuery(id+"F0.wireOp",EDGE,"E2.0.14.2"),sQuery(id+"F0.wireOp",EDGE,"E2.0.14.3"),sQuery(id+"F0.wireOp",EDGE,"E2.0.15.0"),sQuery(id+"F0.wireOp",EDGE,"E2.0.15.1"),sQuery(id+"F0.wireOp",EDGE,"E2.0.15.2"),sQuery(id+"F0.wireOp",EDGE,"E2.0.15.3"),sQuery(id+"F0.wireOp",EDGE,"E2.0.16.0"),sQuery(id+"F0.wireOp",EDGE,"E2.0.16.1"),sQuery(id+"F0.wireOp",EDGE,"E2.0.16.2"),sQuery(id+"F0.wireOp",EDGE,"E2.0.16.3"),sQuery(id+"F0.wireOp",EDGE,"E2.0.17.0"),sQuery(id+"F0.wireOp",EDGE,"E2.0.17.1"),sQuery(id+"F0.wireOp",EDGE,"E2.0.17.2"),sQuery(id+"F0.wireOp",EDGE,"E2.0.17.3"),sQuery(id+"F0.wireOp",EDGE,"E2.0.18.0"),sQuery(id+"F0.wireOp",EDGE,"E2.0.18.1"),sQuery(id+"F0.wireOp",EDGE,"E2.0.18.2"),sQuery(id+"F0.wireOp",EDGE,"E2.0.18.3"),sQuery(id+"F0.wireOp",EDGE,"E2.0.19.0"),sQuery(id+"F0.wireOp",EDGE,"E2.0.19.1"),sQuery(id+"F0.wireOp",EDGE,"E2.0.19.2"),sQuery(id+"F0.wireOp",EDGE,"E2.0.19.3"),sQuery(id+"F0.wireOp",EDGE,"E2.0.20.0"),sQuery(id+"F0.wireOp",EDGE,"E2.0.20.1"),sQuery(id+"F0.wireOp",EDGE,"E2.0.20.2"),sQuery(id+"F0.wireOp",EDGE,"E2.0.20.3"),sQuery(id+"F0.wireOp",EDGE,"E2.0.21.0"),sQuery(id+"F0.wireOp",EDGE,"E2.0.21.1"),sQuery(id+"F0.wireOp",EDGE,"E2.0.21.2"),sQuery(id+"F0.wireOp",EDGE,"E2.0.21.3"),sQuery(id+"F0.wireOp",EDGE,"E2.0.22.0"),sQuery(id+"F0.wireOp",EDGE,"E2.0.22.1"),sQuery(id+"F0.wireOp",EDGE,"E2.0.22.2"),sQuery(id+"F0.wireOp",EDGE,"E2.0.22.3"),sQuery(id+"F0.wireOp",EDGE,"E2.0.23.0"),sQuery(id+"F0.wireOp",EDGE,"E2.0.23.1"),sQuery(id+"F0.wireOp",EDGE,"E2.0.23.2"),sQuery(id+"F0.wireOp",EDGE,"E2.0.23.3"),sQuery(id+"F0.wireOp",EDGE,"E2.0.24.0"),sQuery(id+"F0.wireOp",EDGE,"E2.0.24.1"),sQuery(id+"F0.wireOp",EDGE,"E2.0.24.2"),sQuery(id+"F0.wireOp",EDGE,"E2.0.24.3"),sQuery(id+"F0.wireOp",EDGE,"E2.0.25.0"),sQuery(id+"F0.wireOp",EDGE,"E2.0.25.1"),sQuery(id+"F0.wireOp",EDGE,"E2.0.25.2"),sQuery(id+"F0.wireOp",EDGE,"E2.0.25.3"),sQuery(id+"F0.wireOp",EDGE,"E2.1.0.0"),sQuery(id+"F0.wireOp",EDGE,"E2.1.0.1"),sQuery(id+"F0.wireOp",EDGE,"E2.1.0.2"),sQuery(id+"F0.wireOp",EDGE,"E2.1.0.3"),sQuery(id+"F0.wireOp",EDGE,"E2.1.1.0"),sQuery(id+"F0.wireOp",EDGE,"E2.1.1.1"),sQuery(id+"F0.wireOp",EDGE,"E2.1.1.2"),sQuery(id+"F0.wireOp",EDGE,"E2.1.1.3"),sQuery(id+"F0.wireOp",EDGE,"E2.1.2.0"),sQuery(id+"F0.wireOp",EDGE,"E2.1.2.1"),sQuery(id+"F0.wireOp",EDGE,"E2.1.2.2"),sQuery(id+"F0.wireOp",EDGE,"E2.1.2.3"),sQuery(id+"F0.wireOp",EDGE,"E2.1.3.0"),sQuery(id+"F0.wireOp",EDGE,"E2.1.3.1"),sQuery(id+"F0.wireOp",EDGE,"E2.1.3.2"),sQuery(id+"F0.wireOp",EDGE,"E2.1.3.3"),sQuery(id+"F0.wireOp",EDGE,"E2.1.4.0"),sQuery(id+"F0.wireOp",EDGE,"E2.1.4.1"),sQuery(id+"F0.wireOp",EDGE,"E2.1.4.2"),sQuery(id+"F0.wireOp",EDGE,"E2.1.4.3"),sQuery(id+"F0.wireOp",EDGE,"E2.1.5.0"),sQuery(id+"F0.wireOp",EDGE,"E2.1.5.1"),sQuery(id+"F0.wireOp",EDGE,"E2.1.5.2"),sQuery(id+"F0.wireOp",EDGE,"E2.1.5.3"),sQuery(id+"F0.wireOp",EDGE,"E2.1.6.0"),sQuery(id+"F0.wireOp",EDGE,"E2.1.6.1"),sQuery(id+"F0.wireOp",EDGE,"E2.1.6.2"),sQuery(id+"F0.wireOp",EDGE,"E2.1.6.3"),sQuery(id+"F0.wireOp",EDGE,"E2.1.7.0"),sQuery(id+"F0.wireOp",EDGE,"E2.1.7.1"),sQuery(id+"F0.wireOp",EDGE,"E2.1.7.2"),sQuery(id+"F0.wireOp",EDGE,"E2.1.7.3"),sQuery(id+"F0.wireOp",EDGE,"E2.1.8.0"),sQuery(id+"F0.wireOp",EDGE,"E2.1.8.1"),sQuery(id+"F0.wireOp",EDGE,"E2.1.8.2"),sQuery(id+"F0.wireOp",EDGE,"E2.1.8.3"),sQuery(id+"F0.wireOp",EDGE,"E2.1.9.0"),sQuery(id+"F0.wireOp",EDGE,"E2.1.9.1"),sQuery(id+"F0.wireOp",EDGE,"E2.1.9.2"),sQuery(id+"F0.wireOp",EDGE,"E2.1.9.3"),sQuery(id+"F0.wireOp",EDGE,"E2.1.10.0"),sQuery(id+"F0.wireOp",EDGE,"E2.1.10.1"),sQuery(id+"F0.wireOp",EDGE,"E2.1.10.2"),sQuery(id+"F0.wireOp",EDGE,"E2.1.10.3"),sQuery(id+"F0.wireOp",EDGE,"E2.1.11.0"),sQuery(id+"F0.wireOp",EDGE,"E2.1.11.1"),sQuery(id+"F0.wireOp",EDGE,"E2.1.11.2"),sQuery(id+"F0.wireOp",EDGE,"E2.1.11.3"),sQuery(id+"F0.wireOp",EDGE,"E2.1.12.0"),sQuery(id+"F0.wireOp",EDGE,"E2.1.12.1"),sQuery(id+"F0.wireOp",EDGE,"E2.1.12.2"),sQuery(id+"F0.wireOp",EDGE,"E2.1.12.3"),sQuery(id+"F0.wireOp",EDGE,"E2.1.13.0"),sQuery(id+"F0.wireOp",EDGE,"E2.1.13.1"),sQuery(id+"F0.wireOp",EDGE,"E2.1.13.2"),sQuery(id+"F0.wireOp",EDGE,"E2.1.13.3"),sQuery(id+"F0.wireOp",EDGE,"E2.1.14.0"),sQuery(id+"F0.wireOp",EDGE,"E2.1.14.1"),sQuery(id+"F0.wireOp",EDGE,"E2.1.14.2"),sQuery(id+"F0.wireOp",EDGE,"E2.1.14.3"),sQuery(id+"F0.wireOp",EDGE,"E2.1.15.0"),sQuery(id+"F0.wireOp",EDGE,"E2.1.15.1"),sQuery(id+"F0.wireOp",EDGE,"E2.1.15.2"),sQuery(id+"F0.wireOp",EDGE,"E2.1.15.3"),sQuery(id+"F0.wireOp",EDGE,"E2.1.16.0"),sQuery(id+"F0.wireOp",EDGE,"E2.1.16.1"),sQuery(id+"F0.wireOp",EDGE,"E2.1.16.2"),sQuery(id+"F0.wireOp",EDGE,"E2.1.16.3"),sQuery(id+"F0.wireOp",EDGE,"E2.1.17.0"),sQuery(id+"F0.wireOp",EDGE,"E2.1.17.1"),sQuery(id+"F0.wireOp",EDGE,"E2.1.17.2"),sQuery(id+"F0.wireOp",EDGE,"E2.1.17.3"),sQuery(id+"F0.wireOp",EDGE,"E2.1.18.0"),sQuery(id+"F0.wireOp",EDGE,"E2.1.18.1"),sQuery(id+"F0.wireOp",EDGE,"E2.1.18.2"),sQuery(id+"F0.wireOp",EDGE,"E2.1.18.3"),sQuery(id+"F0.wireOp",EDGE,"E2.1.19.0"),sQuery(id+"F0.wireOp",EDGE,"E2.1.19.1"),sQuery(id+"F0.wireOp",EDGE,"E2.1.19.2"),sQuery(id+"F0.wireOp",EDGE,"E2.1.19.3"),sQuery(id+"F0.wireOp",EDGE,"E2.1.20.0"),sQuery(id+"F0.wireOp",EDGE,"E2.1.20.1"),sQuery(id+"F0.wireOp",EDGE,"E2.1.20.2"),sQuery(id+"F0.wireOp",EDGE,"E2.1.20.3"),sQuery(id+"F0.wireOp",EDGE,"E2.1.21.0"),sQuery(id+"F0.wireOp",EDGE,"E2.1.21.1"),sQuery(id+"F0.wireOp",EDGE,"E2.1.21.2"),sQuery(id+"F0.wireOp",EDGE,"E2.1.21.3"),sQuery(id+"F0.wireOp",EDGE,"E2.1.22.0"),sQuery(id+"F0.wireOp",EDGE,"E2.1.22.1"),sQuery(id+"F0.wireOp",EDGE,"E2.1.22.2"),sQuery(id+"F0.wireOp",EDGE,"E2.1.22.3"),sQuery(id+"F0.wireOp",EDGE,"E2.1.23.0"),sQuery(id+"F0.wireOp",EDGE,"E2.1.23.1"),sQuery(id+"F0.wireOp",EDGE,"E2.1.23.2"),sQuery(id+"F0.wireOp",EDGE,"E2.1.23.3"),sQuery(id+"F0.wireOp",EDGE,"E2.1.24.0"),sQuery(id+"F0.wireOp",EDGE,"E2.1.24.1"),sQuery(id+"F0.wireOp",EDGE,"E2.1.24.2"),sQuery(id+"F0.wireOp",EDGE,"E2.1.24.3"),sQuery(id+"F0.wireOp",EDGE,"E2.1.25.0"),sQuery(id+"F0.wireOp",EDGE,"E2.1.25.1"),sQuery(id+"F0.wireOp",EDGE,"E2.1.25.2"),sQuery(id+"F0.wireOp",EDGE,"E2.1.25.3"),sQuery(id+"F0.wireOp",EDGE,"E2.2.0.0"),sQuery(id+"F0.wireOp",EDGE,"E2.2.0.1"),sQuery(id+"F0.wireOp",EDGE,"E2.2.0.2"),sQuery(id+"F0.wireOp",EDGE,"E2.2.0.3"),sQuery(id+"F0.wireOp",EDGE,"E2.2.1.0"),sQuery(id+"F0.wireOp",EDGE,"E2.2.1.1"),sQuery(id+"F0.wireOp",EDGE,"E2.2.1.2"),sQuery(id+"F0.wireOp",EDGE,"E2.2.1.3"),sQuery(id+"F0.wireOp",EDGE,"E2.2.2.0"),sQuery(id+"F0.wireOp",EDGE,"E2.2.2.1"),sQuery(id+"F0.wireOp",EDGE,"E2.2.2.2"),sQuery(id+"F0.wireOp",EDGE,"E2.2.2.3"),sQuery(id+"F0.wireOp",EDGE,"E2.2.3.0"),sQuery(id+"F0.wireOp",EDGE,"E2.2.3.1"),sQuery(id+"F0.wireOp",EDGE,"E2.2.3.2"),sQuery(id+"F0.wireOp",EDGE,"E2.2.3.3"),sQuery(id+"F0.wireOp",EDGE,"E2.2.4.0"),sQuery(id+"F0.wireOp",EDGE,"E2.2.4.1"),sQuery(id+"F0.wireOp",EDGE,"E2.2.4.2"),sQuery(id+"F0.wireOp",EDGE,"E2.2.4.3"),sQuery(id+"F0.wireOp",EDGE,"E2.2.5.0"),sQuery(id+"F0.wireOp",EDGE,"E2.2.5.1"),sQuery(id+"F0.wireOp",EDGE,"E2.2.5.2"),sQuery(id+"F0.wireOp",EDGE,"E2.2.5.3"),sQuery(id+"F0.wireOp",EDGE,"E2.2.6.0"),sQuery(id+"F0.wireOp",EDGE,"E2.2.6.1"),sQuery(id+"F0.wireOp",EDGE,"E2.2.6.2"),sQuery(id+"F0.wireOp",EDGE,"E2.2.6.3"),sQuery(id+"F0.wireOp",EDGE,"E2.2.7.0"),sQuery(id+"F0.wireOp",EDGE,"E2.2.7.1"),sQuery(id+"F0.wireOp",EDGE,"E2.2.7.2"),sQuery(id+"F0.wireOp",EDGE,"E2.2.7.3"),sQuery(id+"F0.wireOp",EDGE,"E2.2.8.0"),sQuery(id+"F0.wireOp",EDGE,"E2.2.8.1"),sQuery(id+"F0.wireOp",EDGE,"E2.2.8.2"),sQuery(id+"F0.wireOp",EDGE,"E2.2.8.3"),sQuery(id+"F0.wireOp",EDGE,"E2.2.9.0"),sQuery(id+"F0.wireOp",EDGE,"E2.2.9.1"),sQuery(id+"F0.wireOp",EDGE,"E2.2.9.2"),sQuery(id+"F0.wireOp",EDGE,"E2.2.9.3"),sQuery(id+"F0.wireOp",EDGE,"E2.2.10.0"),sQuery(id+"F0.wireOp",EDGE,"E2.2.10.1"),sQuery(id+"F0.wireOp",EDGE,"E2.2.10.2"),sQuery(id+"F0.wireOp",EDGE,"E2.2.10.3"),sQuery(id+"F0.wireOp",EDGE,"E2.2.11.0"),sQuery(id+"F0.wireOp",EDGE,"E2.2.11.1"),sQuery(id+"F0.wireOp",EDGE,"E2.2.11.2"),sQuery(id+"F0.wireOp",EDGE,"E2.2.11.3"),sQuery(id+"F0.wireOp",EDGE,"E2.2.12.0"),sQuery(id+"F0.wireOp",EDGE,"E2.2.12.1"),sQuery(id+"F0.wireOp",EDGE,"E2.2.12.2"),sQuery(id+"F0.wireOp",EDGE,"E2.2.12.3"),sQuery(id+"F0.wireOp",EDGE,"E2.2.13.0"),sQuery(id+"F0.wireOp",EDGE,"E2.2.13.1"),sQuery(id+"F0.wireOp",EDGE,"E2.2.13.2"),sQuery(id+"F0.wireOp",EDGE,"E2.2.13.3"),sQuery(id+"F0.wireOp",EDGE,"E2.2.14.0"),sQuery(id+"F0.wireOp",EDGE,"E2.2.14.1"),sQuery(id+"F0.wireOp",EDGE,"E2.2.14.2"),sQuery(id+"F0.wireOp",EDGE,"E2.2.14.3"),sQuery(id+"F0.wireOp",EDGE,"E2.2.15.0"),sQuery(id+"F0.wireOp",EDGE,"E2.2.15.1"),sQuery(id+"F0.wireOp",EDGE,"E2.2.15.2"),sQuery(id+"F0.wireOp",EDGE,"E2.2.15.3"),sQuery(id+"F0.wireOp",EDGE,"E2.2.16.0"),sQuery(id+"F0.wireOp",EDGE,"E2.2.16.1"),sQuery(id+"F0.wireOp",EDGE,"E2.2.16.2"),sQuery(id+"F0.wireOp",EDGE,"E2.2.16.3"),sQuery(id+"F0.wireOp",EDGE,"E2.2.17.0"),sQuery(id+"F0.wireOp",EDGE,"E2.2.17.1"),sQuery(id+"F0.wireOp",EDGE,"E2.2.17.2"),sQuery(id+"F0.wireOp",EDGE,"E2.2.17.3"),sQuery(id+"F0.wireOp",EDGE,"E2.2.18.0"),sQuery(id+"F0.wireOp",EDGE,"E2.2.18.1"),sQuery(id+"F0.wireOp",EDGE,"E2.2.18.2"),sQuery(id+"F0.wireOp",EDGE,"E2.2.18.3"),sQuery(id+"F0.wireOp",EDGE,"E2.2.19.0"),sQuery(id+"F0.wireOp",EDGE,"E2.2.19.1"),sQuery(id+"F0.wireOp",EDGE,"E2.2.19.2"),sQuery(id+"F0.wireOp",EDGE,"E2.2.19.3"),sQuery(id+"F0.wireOp",EDGE,"E2.2.20.0"),sQuery(id+"F0.wireOp",EDGE,"E2.2.20.1"),sQuery(id+"F0.wireOp",EDGE,"E2.2.20.2"),sQuery(id+"F0.wireOp",EDGE,"E2.2.20.3"),sQuery(id+"F0.wireOp",EDGE,"E2.2.21.0"),sQuery(id+"F0.wireOp",EDGE,"E2.2.21.1"),sQuery(id+"F0.wireOp",EDGE,"E2.2.21.2"),sQuery(id+"F0.wireOp",EDGE,"E2.2.21.3"),sQuery(id+"F0.wireOp",EDGE,"E2.2.22.0"),sQuery(id+"F0.wireOp",EDGE,"E2.2.22.1"),sQuery(id+"F0.wireOp",EDGE,"E2.2.22.2"),sQuery(id+"F0.wireOp",EDGE,"E2.2.22.3"),sQuery(id+"F0.wireOp",EDGE,"E2.2.23.0"),sQuery(id+"F0.wireOp",EDGE,"E2.2.23.1"),sQuery(id+"F0.wireOp",EDGE,"E2.2.23.2"),sQuery(id+"F0.wireOp",EDGE,"E2.2.23.3"),sQuery(id+"F0.wireOp",EDGE,"E2.2.24.0"),sQuery(id+"F0.wireOp",EDGE,"E2.2.24.1"),sQuery(id+"F0.wireOp",EDGE,"E2.2.24.2"),sQuery(id+"F0.wireOp",EDGE,"E2.2.24.3"),sQuery(id+"F0.wireOp",EDGE,"E2.2.25.0"),sQuery(id+"F0.wireOp",EDGE,"E2.2.25.1"),sQuery(id+"F0.wireOp",EDGE,"E2.2.25.2"),sQuery(id+"F0.wireOp",EDGE,"E2.2.25.3"),sQuery(id+"F0.wireOp",EDGE,"E2.3.0.0"),sQuery(id+"F0.wireOp",EDGE,"E2.3.0.1"),sQuery(id+"F0.wireOp",EDGE,"E2.3.0.2"),sQuery(id+"F0.wireOp",EDGE,"E2.3.0.3"),sQuery(id+"F0.wireOp",EDGE,"E2.3.1.0"),sQuery(id+"F0.wireOp",EDGE,"E2.3.1.1"),sQuery(id+"F0.wireOp",EDGE,"E2.3.1.2"),sQuery(id+"F0.wireOp",EDGE,"E2.3.1.3"),sQuery(id+"F0.wireOp",EDGE,"E2.3.2.0"),sQuery(id+"F0.wireOp",EDGE,"E2.3.2.1"),sQuery(id+"F0.wireOp",EDGE,"E2.3.2.2"),sQuery(id+"F0.wireOp",EDGE,"E2.3.2.3"),sQuery(id+"F0.wireOp",EDGE,"E2.3.3.0"),sQuery(id+"F0.wireOp",EDGE,"E2.3.3.1"),sQuery(id+"F0.wireOp",EDGE,"E2.3.3.2"),sQuery(id+"F0.wireOp",EDGE,"E2.3.3.3"),sQuery(id+"F0.wireOp",EDGE,"E2.3.4.0"),sQuery(id+"F0.wireOp",EDGE,"E2.3.4.1"),sQuery(id+"F0.wireOp",EDGE,"E2.3.4.2"),sQuery(id+"F0.wireOp",EDGE,"E2.3.4.3"),sQuery(id+"F0.wireOp",EDGE,"E2.3.5.0"),sQuery(id+"F0.wireOp",EDGE,"E2.3.5.1"),sQuery(id+"F0.wireOp",EDGE,"E2.3.5.2"),sQuery(id+"F0.wireOp",EDGE,"E2.3.5.3"),sQuery(id+"F0.wireOp",EDGE,"E2.3.6.0"),sQuery(id+"F0.wireOp",EDGE,"E2.3.6.1"),sQuery(id+"F0.wireOp",EDGE,"E2.3.6.2"),sQuery(id+"F0.wireOp",EDGE,"E2.3.6.3"),sQuery(id+"F0.wireOp",EDGE,"E2.3.7.0"),sQuery(id+"F0.wireOp",EDGE,"E2.3.7.1"),sQuery(id+"F0.wireOp",EDGE,"E2.3.7.2"),sQuery(id+"F0.wireOp",EDGE,"E2.3.7.3"),sQuery(id+"F0.wireOp",EDGE,"E2.3.8.0"),sQuery(id+"F0.wireOp",EDGE,"E2.3.8.1"),sQuery(id+"F0.wireOp",EDGE,"E2.3.8.2"),sQuery(id+"F0.wireOp",EDGE,"E2.3.8.3"),sQuery(id+"F0.wireOp",EDGE,"E2.3.9.0"),sQuery(id+"F0.wireOp",EDGE,"E2.3.9.1"),sQuery(id+"F0.wireOp",EDGE,"E2.3.9.2"),sQuery(id+"F0.wireOp",EDGE,"E2.3.9.3"),sQuery(id+"F0.wireOp",EDGE,"E2.3.10.0"),sQuery(id+"F0.wireOp",EDGE,"E2.3.10.1"),sQuery(id+"F0.wireOp",EDGE,"E2.3.10.2"),sQuery(id+"F0.wireOp",EDGE,"E2.3.10.3"),sQuery(id+"F0.wireOp",EDGE,"E2.3.11.0"),sQuery(id+"F0.wireOp",EDGE,"E2.3.11.1"),sQuery(id+"F0.wireOp",EDGE,"E2.3.11.2"),sQuery(id+"F0.wireOp",EDGE,"E2.3.11.3"),sQuery(id+"F0.wireOp",EDGE,"E2.3.12.0"),sQuery(id+"F0.wireOp",EDGE,"E2.3.12.1"),sQuery(id+"F0.wireOp",EDGE,"E2.3.12.2"),sQuery(id+"F0.wireOp",EDGE,"E2.3.12.3"),sQuery(id+"F0.wireOp",EDGE,"E2.3.13.0"),sQuery(id+"F0.wireOp",EDGE,"E2.3.13.1"),sQuery(id+"F0.wireOp",EDGE,"E2.3.13.2"),sQuery(id+"F0.wireOp",EDGE,"E2.3.13.3"),sQuery(id+"F0.wireOp",EDGE,"E2.3.14.0"),sQuery(id+"F0.wireOp",EDGE,"E2.3.14.1"),sQuery(id+"F0.wireOp",EDGE,"E2.3.14.2"),sQuery(id+"F0.wireOp",EDGE,"E2.3.14.3"),sQuery(id+"F0.wireOp",EDGE,"E2.3.15.0"),sQuery(id+"F0.wireOp",EDGE,"E2.3.15.1"),sQuery(id+"F0.wireOp",EDGE,"E2.3.15.2"),sQuery(id+"F0.wireOp",EDGE,"E2.3.15.3"),sQuery(id+"F0.wireOp",EDGE,"E2.3.16.0"),sQuery(id+"F0.wireOp",EDGE,"E2.3.16.1"),sQuery(id+"F0.wireOp",EDGE,"E2.3.16.2"),sQuery(id+"F0.wireOp",EDGE,"E2.3.16.3"),sQuery(id+"F0.wireOp",EDGE,"E2.3.17.0"),sQuery(id+"F0.wireOp",EDGE,"E2.3.17.1"),sQuery(id+"F0.wireOp",EDGE,"E2.3.17.2"),sQuery(id+"F0.wireOp",EDGE,"E2.3.17.3"),sQuery(id+"F0.wireOp",EDGE,"E2.3.18.0"),sQuery(id+"F0.wireOp",EDGE,"E2.3.18.1"),sQuery(id+"F0.wireOp",EDGE,"E2.3.18.2"),sQuery(id+"F0.wireOp",EDGE,"E2.3.18.3"),sQuery(id+"F0.wireOp",EDGE,"E2.3.19.0"),sQuery(id+"F0.wireOp",EDGE,"E2.3.19.1"),sQuery(id+"F0.wireOp",EDGE,"E2.3.19.2"),sQuery(id+"F0.wireOp",EDGE,"E2.3.19.3"),sQuery(id+"F0.wireOp",EDGE,"E2.3.20.0"),sQuery(id+"F0.wireOp",EDGE,"E2.3.20.1"),sQuery(id+"F0.wireOp",EDGE,"E2.3.20.2"),sQuery(id+"F0.wireOp",EDGE,"E2.3.20.3"),sQuery(id+"F0.wireOp",EDGE,"E2.3.21.0"),sQuery(id+"F0.wireOp",EDGE,"E2.3.21.1"),sQuery(id+"F0.wireOp",EDGE,"E2.3.21.2"),sQuery(id+"F0.wireOp",EDGE,"E2.3.21.3"),sQuery(id+"F0.wireOp",EDGE,"E2.3.22.0"),sQuery(id+"F0.wireOp",EDGE,"E2.3.22.1"),sQuery(id+"F0.wireOp",EDGE,"E2.3.22.2"),sQuery(id+"F0.wireOp",EDGE,"E2.3.22.3"),sQuery(id+"F0.wireOp",EDGE,"E2.3.23.0"),sQuery(id+"F0.wireOp",EDGE,"E2.3.23.1"),sQuery(id+"F0.wireOp",EDGE,"E2.3.23.2"),sQuery(id+"F0.wireOp",EDGE,"E2.3.23.3"),sQuery(id+"F0.wireOp",EDGE,"E2.3.24.0"),sQuery(id+"F0.wireOp",EDGE,"E2.3.24.1"),sQuery(id+"F0.wireOp",EDGE,"E2.3.24.2"),sQuery(id+"F0.wireOp",EDGE,"E2.3.24.3"),sQuery(id+"F0.wireOp",EDGE,"E2.3.25.0"),sQuery(id+"F0.wireOp",EDGE,"E2.3.25.1"),sQuery(id+"F0.wireOp",EDGE,"E2.3.25.2"),sQuery(id+"F0.wireOp",EDGE,"E2.3.25.3"),sQuery(id+"F0.wireOp",EDGE,"E2.4.0.0"),sQuery(id+"F0.wireOp",EDGE,"E2.4.0.1"),sQuery(id+"F0.wireOp",EDGE,"E2.4.0.2"),sQuery(id+"F0.wireOp",EDGE,"E2.4.0.3"),sQuery(id+"F0.wireOp",EDGE,"E2.4.1.0"),sQuery(id+"F0.wireOp",EDGE,"E2.4.1.1"),sQuery(id+"F0.wireOp",EDGE,"E2.4.1.2"),sQuery(id+"F0.wireOp",EDGE,"E2.4.1.3"),sQuery(id+"F0.wireOp",EDGE,"E2.4.2.0"),sQuery(id+"F0.wireOp",EDGE,"E2.4.2.1"),sQuery(id+"F0.wireOp",EDGE,"E2.4.2.2"),sQuery(id+"F0.wireOp",EDGE,"E2.4.2.3"),sQuery(id+"F0.wireOp",EDGE,"E2.4.3.0"),sQuery(id+"F0.wireOp",EDGE,"E2.4.3.1"),sQuery(id+"F0.wireOp",EDGE,"E2.4.3.2"),sQuery(id+"F0.wireOp",EDGE,"E2.4.3.3"),sQuery(id+"F0.wireOp",EDGE,"E2.4.4.0"),sQuery(id+"F0.wireOp",EDGE,"E2.4.4.1"),sQuery(id+"F0.wireOp",EDGE,"E2.4.4.2"),sQuery(id+"F0.wireOp",EDGE,"E2.4.4.3"),sQuery(id+"F0.wireOp",EDGE,"E2.4.5.0"),sQuery(id+"F0.wireOp",EDGE,"E2.4.5.1"),sQuery(id+"F0.wireOp",EDGE,"E2.4.5.2"),sQuery(id+"F0.wireOp",EDGE,"E2.4.5.3"),sQuery(id+"F0.wireOp",EDGE,"E2.4.6.0"),sQuery(id+"F0.wireOp",EDGE,"E2.4.6.1"),sQuery(id+"F0.wireOp",EDGE,"E2.4.6.2"),sQuery(id+"F0.wireOp",EDGE,"E2.4.6.3"),sQuery(id+"F0.wireOp",EDGE,"E2.4.7.0"),sQuery(id+"F0.wireOp",EDGE,"E2.4.7.1"),sQuery(id+"F0.wireOp",EDGE,"E2.4.7.2"),sQuery(id+"F0.wireOp",EDGE,"E2.4.7.3"),sQuery(id+"F0.wireOp",EDGE,"E2.4.8.0"),sQuery(id+"F0.wireOp",EDGE,"E2.4.8.1"),sQuery(id+"F0.wireOp",EDGE,"E2.4.8.2"),sQuery(id+"F0.wireOp",EDGE,"E2.4.8.3"),sQuery(id+"F0.wireOp",EDGE,"E2.4.9.0"),sQuery(id+"F0.wireOp",EDGE,"E2.4.9.1"),sQuery(id+"F0.wireOp",EDGE,"E2.4.9.2"),sQuery(id+"F0.wireOp",EDGE,"E2.4.9.3"),sQuery(id+"F0.wireOp",EDGE,"E2.4.10.0"),sQuery(id+"F0.wireOp",EDGE,"E2.4.10.1"),sQuery(id+"F0.wireOp",EDGE,"E2.4.10.2"),sQuery(id+"F0.wireOp",EDGE,"E2.4.10.3"),sQuery(id+"F0.wireOp",EDGE,"E2.4.11.0"),sQuery(id+"F0.wireOp",EDGE,"E2.4.11.1"),sQuery(id+"F0.wireOp",EDGE,"E2.4.11.2"),sQuery(id+"F0.wireOp",EDGE,"E2.4.11.3"),sQuery(id+"F0.wireOp",EDGE,"E2.4.12.0"),sQuery(id+"F0.wireOp",EDGE,"E2.4.12.1"),sQuery(id+"F0.wireOp",EDGE,"E2.4.12.2"),sQuery(id+"F0.wireOp",EDGE,"E2.4.12.3"),sQuery(id+"F0.wireOp",EDGE,"E2.4.13.0"),sQuery(id+"F0.wireOp",EDGE,"E2.4.13.1"),sQuery(id+"F0.wireOp",EDGE,"E2.4.13.2"),sQuery(id+"F0.wireOp",EDGE,"E2.4.13.3"),sQuery(id+"F0.wireOp",EDGE,"E2.4.14.0"),sQuery(id+"F0.wireOp",EDGE,"E2.4.14.1"),sQuery(id+"F0.wireOp",EDGE,"E2.4.14.2"),sQuery(id+"F0.wireOp",EDGE,"E2.4.14.3"),sQuery(id+"F0.wireOp",EDGE,"E2.4.15.0"),sQuery(id+"F0.wireOp",EDGE,"E2.4.15.1"),sQuery(id+"F0.wireOp",EDGE,"E2.4.15.2"),sQuery(id+"F0.wireOp",EDGE,"E2.4.15.3"),sQuery(id+"F0.wireOp",EDGE,"E2.4.16.0"),sQuery(id+"F0.wireOp",EDGE,"E2.4.16.1"),sQuery(id+"F0.wireOp",EDGE,"E2.4.16.2"),sQuery(id+"F0.wireOp",EDGE,"E2.4.16.3"),sQuery(id+"F0.wireOp",EDGE,"E2.4.17.0"),sQuery(id+"F0.wireOp",EDGE,"E2.4.17.1"),sQuery(id+"F0.wireOp",EDGE,"E2.4.17.2"),sQuery(id+"F0.wireOp",EDGE,"E2.4.17.3"),sQuery(id+"F0.wireOp",EDGE,"E2.4.18.0"),sQuery(id+"F0.wireOp",EDGE,"E2.4.18.1"),sQuery(id+"F0.wireOp",EDGE,"E2.4.18.2"),sQuery(id+"F0.wireOp",EDGE,"E2.4.18.3"),sQuery(id+"F0.wireOp",EDGE,"E2.4.19.0"),sQuery(id+"F0.wireOp",EDGE,"E2.4.19.1"),sQuery(id+"F0.wireOp",EDGE,"E2.4.19.2"),sQuery(id+"F0.wireOp",EDGE,"E2.4.19.3"),sQuery(id+"F0.wireOp",EDGE,"E2.4.20.0"),sQuery(id+"F0.wireOp",EDGE,"E2.4.20.1"),sQuery(id+"F0.wireOp",EDGE,"E2.4.20.2"),sQuery(id+"F0.wireOp",EDGE,"E2.4.20.3"),sQuery(id+"F0.wireOp",EDGE,"E2.4.21.0"),sQuery(id+"F0.wireOp",EDGE,"E2.4.21.1"),sQuery(id+"F0.wireOp",EDGE,"E2.4.21.2"),sQuery(id+"F0.wireOp",EDGE,"E2.4.21.3"),sQuery(id+"F0.wireOp",EDGE,"E2.4.22.0"),sQuery(id+"F0.wireOp",EDGE,"E2.4.22.1"),sQuery(id+"F0.wireOp",EDGE,"E2.4.22.2"),sQuery(id+"F0.wireOp",EDGE,"E2.4.22.3"),sQuery(id+"F0.wireOp",EDGE,"E2.4.23.0"),sQuery(id+"F0.wireOp",EDGE,"E2.4.23.1"),sQuery(id+"F0.wireOp",EDGE,"E2.4.23.2"),sQuery(id+"F0.wireOp",EDGE,"E2.4.23.3"),sQuery(id+"F0.wireOp",EDGE,"E2.4.24.0"),sQuery(id+"F0.wireOp",EDGE,"E2.4.24.1"),sQuery(id+"F0.wireOp",EDGE,"E2.4.24.2"),sQuery(id+"F0.wireOp",EDGE,"E2.4.24.3"),sQuery(id+"F0.wireOp",EDGE,"E2.4.25.0"),sQuery(id+"F0.wireOp",EDGE,"E2.4.25.1"),sQuery(id+"F0.wireOp",EDGE,"E2.4.25.2"),sQuery(id+"F0.wireOp",EDGE,"E2.4.25.3")])]});
            var Q1;
            Q1=sQuery(id+"F4.wireOp",EDGE,"E9");
            transform(context, id + "F5", {"entities" : qUnion([Q0]), "transformType" : TransformType.ROTATION, "transformAxis" : qUnion([Q1]), "angle" : 90 * degree, "makeCopy" : false});
        }
        {
            var Q0;
            Q0=makeQuery(id+"F3.boolean.opBoolean","MERGE",FACE,{"derivedFrom":[makeQuery(id+"F1.opExtrude","CAP_FACE",FACE,{"disambiguationData":[OSD([sQuery(id+"F0.wireOp",EDGE,"E0.bottom"),sQuery(id+"F0.wireOp",EDGE,"E0.top"),sQuery(id+"F0.wireOp",EDGE,"E0.left"),sQuery(id+"F0.wireOp",EDGE,"E0.right"),sQuery(id+"F0.wireOp",EDGE,"E1.bottom"),sQuery(id+"F0.wireOp",EDGE,"E1.top"),sQuery(id+"F0.wireOp",EDGE,"E1.left"),sQuery(id+"F0.wireOp",EDGE,"E1.right"),sQuery(id+"F0.wireOp",EDGE,"E2.0.1.0"),sQuery(id+"F0.wireOp",EDGE,"E2.0.1.1"),sQuery(id+"F0.wireOp",EDGE,"E2.0.1.2"),sQuery(id+"F0.wireOp",EDGE,"E2.0.1.3"),sQuery(id+"F0.wireOp",EDGE,"E2.0.2.0"),sQuery(id+"F0.wireOp",EDGE,"E2.0.2.1"),sQuery(id+"F0.wireOp",EDGE,"E2.0.2.2"),sQuery(id+"F0.wireOp",EDGE,"E2.0.2.3"),sQuery(id+"F0.wireOp",EDGE,"E2.0.3.0"),sQuery(id+"F0.wireOp",EDGE,"E2.0.3.1"),sQuery(id+"F0.wireOp",EDGE,"E2.0.3.2"),sQuery(id+"F0.wireOp",EDGE,"E2.0.3.3"),sQuery(id+"F0.wireOp",EDGE,"E2.0.4.0"),sQuery(id+"F0.wireOp",EDGE,"E2.0.4.1"),sQuery(id+"F0.wireOp",EDGE,"E2.0.4.2"),sQuery(id+"F0.wireOp",EDGE,"E2.0.4.3"),sQuery(id+"F0.wireOp",EDGE,"E2.0.5.0"),sQuery(id+"F0.wireOp",EDGE,"E2.0.5.1"),sQuery(id+"F0.wireOp",EDGE,"E2.0.5.2"),sQuery(id+"F0.wireOp",EDGE,"E2.0.5.3"),sQuery(id+"F0.wireOp",EDGE,"E2.0.6.0"),sQuery(id+"F0.wireOp",EDGE,"E2.0.6.1"),sQuery(id+"F0.wireOp",EDGE,"E2.0.6.2"),sQuery(id+"F0.wireOp",EDGE,"E2.0.6.3"),sQuery(id+"F0.wireOp",EDGE,"E2.0.7.0"),sQuery(id+"F0.wireOp",EDGE,"E2.0.7.1"),sQuery(id+"F0.wireOp",EDGE,"E2.0.7.2"),sQuery(id+"F0.wireOp",EDGE,"E2.0.7.3"),sQuery(id+"F0.wireOp",EDGE,"E2.0.8.0"),sQuery(id+"F0.wireOp",EDGE,"E2.0.8.1"),sQuery(id+"F0.wireOp",EDGE,"E2.0.8.2"),sQuery(id+"F0.wireOp",EDGE,"E2.0.8.3"),sQuery(id+"F0.wireOp",EDGE,"E2.0.9.0"),sQuery(id+"F0.wireOp",EDGE,"E2.0.9.1"),sQuery(id+"F0.wireOp",EDGE,"E2.0.9.2"),sQuery(id+"F0.wireOp",EDGE,"E2.0.9.3"),sQuery(id+"F0.wireOp",EDGE,"E2.0.10.0"),sQuery(id+"F0.wireOp",EDGE,"E2.0.10.1"),sQuery(id+"F0.wireOp",EDGE,"E2.0.10.2"),sQuery(id+"F0.wireOp",EDGE,"E2.0.10.3"),sQuery(id+"F0.wireOp",EDGE,"E2.0.11.0"),sQuery(id+"F0.wireOp",EDGE,"E2.0.11.1"),sQuery(id+"F0.wireOp",EDGE,"E2.0.11.2"),sQuery(id+"F0.wireOp",EDGE,"E2.0.11.3"),sQuery(id+"F0.wireOp",EDGE,"E2.0.12.0"),sQuery(id+"F0.wireOp",EDGE,"E2.0.12.1"),sQuery(id+"F0.wireOp",EDGE,"E2.0.12.2"),sQuery(id+"F0.wireOp",EDGE,"E2.0.12.3"),sQuery(id+"F0.wireOp",EDGE,"E2.0.13.0"),sQuery(id+"F0.wireOp",EDGE,"E2.0.13.1"),sQuery(id+"F0.wireOp",EDGE,"E2.0.13.2"),sQuery(id+"F0.wireOp",EDGE,"E2.0.13.3"),sQuery(id+"F0.wireOp",EDGE,"E2.0.14.0"),sQuery(id+"F0.wireOp",EDGE,"E2.0.14.1"),sQuery(id+"F0.wireOp",EDGE,"E2.0.14.2"),sQuery(id+"F0.wireOp",EDGE,"E2.0.14.3"),sQuery(id+"F0.wireOp",EDGE,"E2.0.15.0"),sQuery(id+"F0.wireOp",EDGE,"E2.0.15.1"),sQuery(id+"F0.wireOp",EDGE,"E2.0.15.2"),sQuery(id+"F0.wireOp",EDGE,"E2.0.15.3"),sQuery(id+"F0.wireOp",EDGE,"E2.0.16.0"),sQuery(id+"F0.wireOp",EDGE,"E2.0.16.1"),sQuery(id+"F0.wireOp",EDGE,"E2.0.16.2"),sQuery(id+"F0.wireOp",EDGE,"E2.0.16.3"),sQuery(id+"F0.wireOp",EDGE,"E2.0.17.0"),sQuery(id+"F0.wireOp",EDGE,"E2.0.17.1"),sQuery(id+"F0.wireOp",EDGE,"E2.0.17.2"),sQuery(id+"F0.wireOp",EDGE,"E2.0.17.3"),sQuery(id+"F0.wireOp",EDGE,"E2.0.18.0"),sQuery(id+"F0.wireOp",EDGE,"E2.0.18.1"),sQuery(id+"F0.wireOp",EDGE,"E2.0.18.2"),sQuery(id+"F0.wireOp",EDGE,"E2.0.18.3"),sQuery(id+"F0.wireOp",EDGE,"E2.0.19.0"),sQuery(id+"F0.wireOp",EDGE,"E2.0.19.1"),sQuery(id+"F0.wireOp",EDGE,"E2.0.19.2"),sQuery(id+"F0.wireOp",EDGE,"E2.0.19.3"),sQuery(id+"F0.wireOp",EDGE,"E2.0.20.0"),sQuery(id+"F0.wireOp",EDGE,"E2.0.20.1"),sQuery(id+"F0.wireOp",EDGE,"E2.0.20.2"),sQuery(id+"F0.wireOp",EDGE,"E2.0.20.3"),sQuery(id+"F0.wireOp",EDGE,"E2.0.21.0"),sQuery(id+"F0.wireOp",EDGE,"E2.0.21.1"),sQuery(id+"F0.wireOp",EDGE,"E2.0.21.2"),sQuery(id+"F0.wireOp",EDGE,"E2.0.21.3"),sQuery(id+"F0.wireOp",EDGE,"E2.0.22.0"),sQuery(id+"F0.wireOp",EDGE,"E2.0.22.1"),sQuery(id+"F0.wireOp",EDGE,"E2.0.22.2"),sQuery(id+"F0.wireOp",EDGE,"E2.0.22.3"),sQuery(id+"F0.wireOp",EDGE,"E2.0.23.0"),sQuery(id+"F0.wireOp",EDGE,"E2.0.23.1"),sQuery(id+"F0.wireOp",EDGE,"E2.0.23.2"),sQuery(id+"F0.wireOp",EDGE,"E2.0.23.3"),sQuery(id+"F0.wireOp",EDGE,"E2.0.24.0"),sQuery(id+"F0.wireOp",EDGE,"E2.0.24.1"),sQuery(id+"F0.wireOp",EDGE,"E2.0.24.2"),sQuery(id+"F0.wireOp",EDGE,"E2.0.24.3"),sQuery(id+"F0.wireOp",EDGE,"E2.0.25.0"),sQuery(id+"F0.wireOp",EDGE,"E2.0.25.1"),sQuery(id+"F0.wireOp",EDGE,"E2.0.25.2"),sQuery(id+"F0.wireOp",EDGE,"E2.0.25.3"),sQuery(id+"F0.wireOp",EDGE,"E2.1.0.0"),sQuery(id+"F0.wireOp",EDGE,"E2.1.0.1"),sQuery(id+"F0.wireOp",EDGE,"E2.1.0.2"),sQuery(id+"F0.wireOp",EDGE,"E2.1.0.3"),sQuery(id+"F0.wireOp",EDGE,"E2.1.1.0"),sQuery(id+"F0.wireOp",EDGE,"E2.1.1.1"),sQuery(id+"F0.wireOp",EDGE,"E2.1.1.2"),sQuery(id+"F0.wireOp",EDGE,"E2.1.1.3"),sQuery(id+"F0.wireOp",EDGE,"E2.1.2.0"),sQuery(id+"F0.wireOp",EDGE,"E2.1.2.1"),sQuery(id+"F0.wireOp",EDGE,"E2.1.2.2"),sQuery(id+"F0.wireOp",EDGE,"E2.1.2.3"),sQuery(id+"F0.wireOp",EDGE,"E2.1.3.0"),sQuery(id+"F0.wireOp",EDGE,"E2.1.3.1"),sQuery(id+"F0.wireOp",EDGE,"E2.1.3.2"),sQuery(id+"F0.wireOp",EDGE,"E2.1.3.3"),sQuery(id+"F0.wireOp",EDGE,"E2.1.4.0"),sQuery(id+"F0.wireOp",EDGE,"E2.1.4.1"),sQuery(id+"F0.wireOp",EDGE,"E2.1.4.2"),sQuery(id+"F0.wireOp",EDGE,"E2.1.4.3"),sQuery(id+"F0.wireOp",EDGE,"E2.1.5.0"),sQuery(id+"F0.wireOp",EDGE,"E2.1.5.1"),sQuery(id+"F0.wireOp",EDGE,"E2.1.5.2"),sQuery(id+"F0.wireOp",EDGE,"E2.1.5.3"),sQuery(id+"F0.wireOp",EDGE,"E2.1.6.0"),sQuery(id+"F0.wireOp",EDGE,"E2.1.6.1"),sQuery(id+"F0.wireOp",EDGE,"E2.1.6.2"),sQuery(id+"F0.wireOp",EDGE,"E2.1.6.3"),sQuery(id+"F0.wireOp",EDGE,"E2.1.7.0"),sQuery(id+"F0.wireOp",EDGE,"E2.1.7.1"),sQuery(id+"F0.wireOp",EDGE,"E2.1.7.2"),sQuery(id+"F0.wireOp",EDGE,"E2.1.7.3"),sQuery(id+"F0.wireOp",EDGE,"E2.1.8.0"),sQuery(id+"F0.wireOp",EDGE,"E2.1.8.1"),sQuery(id+"F0.wireOp",EDGE,"E2.1.8.2"),sQuery(id+"F0.wireOp",EDGE,"E2.1.8.3"),sQuery(id+"F0.wireOp",EDGE,"E2.1.9.0"),sQuery(id+"F0.wireOp",EDGE,"E2.1.9.1"),sQuery(id+"F0.wireOp",EDGE,"E2.1.9.2"),sQuery(id+"F0.wireOp",EDGE,"E2.1.9.3"),sQuery(id+"F0.wireOp",EDGE,"E2.1.10.0"),sQuery(id+"F0.wireOp",EDGE,"E2.1.10.1"),sQuery(id+"F0.wireOp",EDGE,"E2.1.10.2"),sQuery(id+"F0.wireOp",EDGE,"E2.1.10.3"),sQuery(id+"F0.wireOp",EDGE,"E2.1.11.0"),sQuery(id+"F0.wireOp",EDGE,"E2.1.11.1"),sQuery(id+"F0.wireOp",EDGE,"E2.1.11.2"),sQuery(id+"F0.wireOp",EDGE,"E2.1.11.3"),sQuery(id+"F0.wireOp",EDGE,"E2.1.12.0"),sQuery(id+"F0.wireOp",EDGE,"E2.1.12.1"),sQuery(id+"F0.wireOp",EDGE,"E2.1.12.2"),sQuery(id+"F0.wireOp",EDGE,"E2.1.12.3"),sQuery(id+"F0.wireOp",EDGE,"E2.1.13.0"),sQuery(id+"F0.wireOp",EDGE,"E2.1.13.1"),sQuery(id+"F0.wireOp",EDGE,"E2.1.13.2"),sQuery(id+"F0.wireOp",EDGE,"E2.1.13.3"),sQuery(id+"F0.wireOp",EDGE,"E2.1.14.0"),sQuery(id+"F0.wireOp",EDGE,"E2.1.14.1"),sQuery(id+"F0.wireOp",EDGE,"E2.1.14.2"),sQuery(id+"F0.wireOp",EDGE,"E2.1.14.3"),sQuery(id+"F0.wireOp",EDGE,"E2.1.15.0"),sQuery(id+"F0.wireOp",EDGE,"E2.1.15.1"),sQuery(id+"F0.wireOp",EDGE,"E2.1.15.2"),sQuery(id+"F0.wireOp",EDGE,"E2.1.15.3"),sQuery(id+"F0.wireOp",EDGE,"E2.1.16.0"),sQuery(id+"F0.wireOp",EDGE,"E2.1.16.1"),sQuery(id+"F0.wireOp",EDGE,"E2.1.16.2"),sQuery(id+"F0.wireOp",EDGE,"E2.1.16.3"),sQuery(id+"F0.wireOp",EDGE,"E2.1.17.0"),sQuery(id+"F0.wireOp",EDGE,"E2.1.17.1"),sQuery(id+"F0.wireOp",EDGE,"E2.1.17.2"),sQuery(id+"F0.wireOp",EDGE,"E2.1.17.3"),sQuery(id+"F0.wireOp",EDGE,"E2.1.18.0"),sQuery(id+"F0.wireOp",EDGE,"E2.1.18.1"),sQuery(id+"F0.wireOp",EDGE,"E2.1.18.2"),sQuery(id+"F0.wireOp",EDGE,"E2.1.18.3"),sQuery(id+"F0.wireOp",EDGE,"E2.1.19.0"),sQuery(id+"F0.wireOp",EDGE,"E2.1.19.1"),sQuery(id+"F0.wireOp",EDGE,"E2.1.19.2"),sQuery(id+"F0.wireOp",EDGE,"E2.1.19.3"),sQuery(id+"F0.wireOp",EDGE,"E2.1.20.0"),sQuery(id+"F0.wireOp",EDGE,"E2.1.20.1"),sQuery(id+"F0.wireOp",EDGE,"E2.1.20.2"),sQuery(id+"F0.wireOp",EDGE,"E2.1.20.3"),sQuery(id+"F0.wireOp",EDGE,"E2.1.21.0"),sQuery(id+"F0.wireOp",EDGE,"E2.1.21.1"),sQuery(id+"F0.wireOp",EDGE,"E2.1.21.2"),sQuery(id+"F0.wireOp",EDGE,"E2.1.21.3"),sQuery(id+"F0.wireOp",EDGE,"E2.1.22.0"),sQuery(id+"F0.wireOp",EDGE,"E2.1.22.1"),sQuery(id+"F0.wireOp",EDGE,"E2.1.22.2"),sQuery(id+"F0.wireOp",EDGE,"E2.1.22.3"),sQuery(id+"F0.wireOp",EDGE,"E2.1.23.0"),sQuery(id+"F0.wireOp",EDGE,"E2.1.23.1"),sQuery(id+"F0.wireOp",EDGE,"E2.1.23.2"),sQuery(id+"F0.wireOp",EDGE,"E2.1.23.3"),sQuery(id+"F0.wireOp",EDGE,"E2.1.24.0"),sQuery(id+"F0.wireOp",EDGE,"E2.1.24.1"),sQuery(id+"F0.wireOp",EDGE,"E2.1.24.2"),sQuery(id+"F0.wireOp",EDGE,"E2.1.24.3"),sQuery(id+"F0.wireOp",EDGE,"E2.1.25.0"),sQuery(id+"F0.wireOp",EDGE,"E2.1.25.1"),sQuery(id+"F0.wireOp",EDGE,"E2.1.25.2"),sQuery(id+"F0.wireOp",EDGE,"E2.1.25.3"),sQuery(id+"F0.wireOp",EDGE,"E2.2.0.0"),sQuery(id+"F0.wireOp",EDGE,"E2.2.0.1"),sQuery(id+"F0.wireOp",EDGE,"E2.2.0.2"),sQuery(id+"F0.wireOp",EDGE,"E2.2.0.3"),sQuery(id+"F0.wireOp",EDGE,"E2.2.1.0"),sQuery(id+"F0.wireOp",EDGE,"E2.2.1.1"),sQuery(id+"F0.wireOp",EDGE,"E2.2.1.2"),sQuery(id+"F0.wireOp",EDGE,"E2.2.1.3"),sQuery(id+"F0.wireOp",EDGE,"E2.2.2.0"),sQuery(id+"F0.wireOp",EDGE,"E2.2.2.1"),sQuery(id+"F0.wireOp",EDGE,"E2.2.2.2"),sQuery(id+"F0.wireOp",EDGE,"E2.2.2.3"),sQuery(id+"F0.wireOp",EDGE,"E2.2.3.0"),sQuery(id+"F0.wireOp",EDGE,"E2.2.3.1"),sQuery(id+"F0.wireOp",EDGE,"E2.2.3.2"),sQuery(id+"F0.wireOp",EDGE,"E2.2.3.3"),sQuery(id+"F0.wireOp",EDGE,"E2.2.4.0"),sQuery(id+"F0.wireOp",EDGE,"E2.2.4.1"),sQuery(id+"F0.wireOp",EDGE,"E2.2.4.2"),sQuery(id+"F0.wireOp",EDGE,"E2.2.4.3"),sQuery(id+"F0.wireOp",EDGE,"E2.2.5.0"),sQuery(id+"F0.wireOp",EDGE,"E2.2.5.1"),sQuery(id+"F0.wireOp",EDGE,"E2.2.5.2"),sQuery(id+"F0.wireOp",EDGE,"E2.2.5.3"),sQuery(id+"F0.wireOp",EDGE,"E2.2.6.0"),sQuery(id+"F0.wireOp",EDGE,"E2.2.6.1"),sQuery(id+"F0.wireOp",EDGE,"E2.2.6.2"),sQuery(id+"F0.wireOp",EDGE,"E2.2.6.3"),sQuery(id+"F0.wireOp",EDGE,"E2.2.7.0"),sQuery(id+"F0.wireOp",EDGE,"E2.2.7.1"),sQuery(id+"F0.wireOp",EDGE,"E2.2.7.2"),sQuery(id+"F0.wireOp",EDGE,"E2.2.7.3"),sQuery(id+"F0.wireOp",EDGE,"E2.2.8.0"),sQuery(id+"F0.wireOp",EDGE,"E2.2.8.1"),sQuery(id+"F0.wireOp",EDGE,"E2.2.8.2"),sQuery(id+"F0.wireOp",EDGE,"E2.2.8.3"),sQuery(id+"F0.wireOp",EDGE,"E2.2.9.0"),sQuery(id+"F0.wireOp",EDGE,"E2.2.9.1"),sQuery(id+"F0.wireOp",EDGE,"E2.2.9.2"),sQuery(id+"F0.wireOp",EDGE,"E2.2.9.3"),sQuery(id+"F0.wireOp",EDGE,"E2.2.10.0"),sQuery(id+"F0.wireOp",EDGE,"E2.2.10.1"),sQuery(id+"F0.wireOp",EDGE,"E2.2.10.2"),sQuery(id+"F0.wireOp",EDGE,"E2.2.10.3"),sQuery(id+"F0.wireOp",EDGE,"E2.2.11.0"),sQuery(id+"F0.wireOp",EDGE,"E2.2.11.1"),sQuery(id+"F0.wireOp",EDGE,"E2.2.11.2"),sQuery(id+"F0.wireOp",EDGE,"E2.2.11.3"),sQuery(id+"F0.wireOp",EDGE,"E2.2.12.0"),sQuery(id+"F0.wireOp",EDGE,"E2.2.12.1"),sQuery(id+"F0.wireOp",EDGE,"E2.2.12.2"),sQuery(id+"F0.wireOp",EDGE,"E2.2.12.3"),sQuery(id+"F0.wireOp",EDGE,"E2.2.13.0"),sQuery(id+"F0.wireOp",EDGE,"E2.2.13.1"),sQuery(id+"F0.wireOp",EDGE,"E2.2.13.2"),sQuery(id+"F0.wireOp",EDGE,"E2.2.13.3"),sQuery(id+"F0.wireOp",EDGE,"E2.2.14.0"),sQuery(id+"F0.wireOp",EDGE,"E2.2.14.1"),sQuery(id+"F0.wireOp",EDGE,"E2.2.14.2"),sQuery(id+"F0.wireOp",EDGE,"E2.2.14.3"),sQuery(id+"F0.wireOp",EDGE,"E2.2.15.0"),sQuery(id+"F0.wireOp",EDGE,"E2.2.15.1"),sQuery(id+"F0.wireOp",EDGE,"E2.2.15.2"),sQuery(id+"F0.wireOp",EDGE,"E2.2.15.3"),sQuery(id+"F0.wireOp",EDGE,"E2.2.16.0"),sQuery(id+"F0.wireOp",EDGE,"E2.2.16.1"),sQuery(id+"F0.wireOp",EDGE,"E2.2.16.2"),sQuery(id+"F0.wireOp",EDGE,"E2.2.16.3"),sQuery(id+"F0.wireOp",EDGE,"E2.2.17.0"),sQuery(id+"F0.wireOp",EDGE,"E2.2.17.1"),sQuery(id+"F0.wireOp",EDGE,"E2.2.17.2"),sQuery(id+"F0.wireOp",EDGE,"E2.2.17.3"),sQuery(id+"F0.wireOp",EDGE,"E2.2.18.0"),sQuery(id+"F0.wireOp",EDGE,"E2.2.18.1"),sQuery(id+"F0.wireOp",EDGE,"E2.2.18.2"),sQuery(id+"F0.wireOp",EDGE,"E2.2.18.3"),sQuery(id+"F0.wireOp",EDGE,"E2.2.19.0"),sQuery(id+"F0.wireOp",EDGE,"E2.2.19.1"),sQuery(id+"F0.wireOp",EDGE,"E2.2.19.2"),sQuery(id+"F0.wireOp",EDGE,"E2.2.19.3"),sQuery(id+"F0.wireOp",EDGE,"E2.2.20.0"),sQuery(id+"F0.wireOp",EDGE,"E2.2.20.1"),sQuery(id+"F0.wireOp",EDGE,"E2.2.20.2"),sQuery(id+"F0.wireOp",EDGE,"E2.2.20.3"),sQuery(id+"F0.wireOp",EDGE,"E2.2.21.0"),sQuery(id+"F0.wireOp",EDGE,"E2.2.21.1"),sQuery(id+"F0.wireOp",EDGE,"E2.2.21.2"),sQuery(id+"F0.wireOp",EDGE,"E2.2.21.3"),sQuery(id+"F0.wireOp",EDGE,"E2.2.22.0"),sQuery(id+"F0.wireOp",EDGE,"E2.2.22.1"),sQuery(id+"F0.wireOp",EDGE,"E2.2.22.2"),sQuery(id+"F0.wireOp",EDGE,"E2.2.22.3"),sQuery(id+"F0.wireOp",EDGE,"E2.2.23.0"),sQuery(id+"F0.wireOp",EDGE,"E2.2.23.1"),sQuery(id+"F0.wireOp",EDGE,"E2.2.23.2"),sQuery(id+"F0.wireOp",EDGE,"E2.2.23.3"),sQuery(id+"F0.wireOp",EDGE,"E2.2.24.0"),sQuery(id+"F0.wireOp",EDGE,"E2.2.24.1"),sQuery(id+"F0.wireOp",EDGE,"E2.2.24.2"),sQuery(id+"F0.wireOp",EDGE,"E2.2.24.3"),sQuery(id+"F0.wireOp",EDGE,"E2.2.25.0"),sQuery(id+"F0.wireOp",EDGE,"E2.2.25.1"),sQuery(id+"F0.wireOp",EDGE,"E2.2.25.2"),sQuery(id+"F0.wireOp",EDGE,"E2.2.25.3"),sQuery(id+"F0.wireOp",EDGE,"E2.3.0.0"),sQuery(id+"F0.wireOp",EDGE,"E2.3.0.1"),sQuery(id+"F0.wireOp",EDGE,"E2.3.0.2"),sQuery(id+"F0.wireOp",EDGE,"E2.3.0.3"),sQuery(id+"F0.wireOp",EDGE,"E2.3.1.0"),sQuery(id+"F0.wireOp",EDGE,"E2.3.1.1"),sQuery(id+"F0.wireOp",EDGE,"E2.3.1.2"),sQuery(id+"F0.wireOp",EDGE,"E2.3.1.3"),sQuery(id+"F0.wireOp",EDGE,"E2.3.2.0"),sQuery(id+"F0.wireOp",EDGE,"E2.3.2.1"),sQuery(id+"F0.wireOp",EDGE,"E2.3.2.2"),sQuery(id+"F0.wireOp",EDGE,"E2.3.2.3"),sQuery(id+"F0.wireOp",EDGE,"E2.3.3.0"),sQuery(id+"F0.wireOp",EDGE,"E2.3.3.1"),sQuery(id+"F0.wireOp",EDGE,"E2.3.3.2"),sQuery(id+"F0.wireOp",EDGE,"E2.3.3.3"),sQuery(id+"F0.wireOp",EDGE,"E2.3.4.0"),sQuery(id+"F0.wireOp",EDGE,"E2.3.4.1"),sQuery(id+"F0.wireOp",EDGE,"E2.3.4.2"),sQuery(id+"F0.wireOp",EDGE,"E2.3.4.3"),sQuery(id+"F0.wireOp",EDGE,"E2.3.5.0"),sQuery(id+"F0.wireOp",EDGE,"E2.3.5.1"),sQuery(id+"F0.wireOp",EDGE,"E2.3.5.2"),sQuery(id+"F0.wireOp",EDGE,"E2.3.5.3"),sQuery(id+"F0.wireOp",EDGE,"E2.3.6.0"),sQuery(id+"F0.wireOp",EDGE,"E2.3.6.1"),sQuery(id+"F0.wireOp",EDGE,"E2.3.6.2"),sQuery(id+"F0.wireOp",EDGE,"E2.3.6.3"),sQuery(id+"F0.wireOp",EDGE,"E2.3.7.0"),sQuery(id+"F0.wireOp",EDGE,"E2.3.7.1"),sQuery(id+"F0.wireOp",EDGE,"E2.3.7.2"),sQuery(id+"F0.wireOp",EDGE,"E2.3.7.3"),sQuery(id+"F0.wireOp",EDGE,"E2.3.8.0"),sQuery(id+"F0.wireOp",EDGE,"E2.3.8.1"),sQuery(id+"F0.wireOp",EDGE,"E2.3.8.2"),sQuery(id+"F0.wireOp",EDGE,"E2.3.8.3"),sQuery(id+"F0.wireOp",EDGE,"E2.3.9.0"),sQuery(id+"F0.wireOp",EDGE,"E2.3.9.1"),sQuery(id+"F0.wireOp",EDGE,"E2.3.9.2"),sQuery(id+"F0.wireOp",EDGE,"E2.3.9.3"),sQuery(id+"F0.wireOp",EDGE,"E2.3.10.0"),sQuery(id+"F0.wireOp",EDGE,"E2.3.10.1"),sQuery(id+"F0.wireOp",EDGE,"E2.3.10.2"),sQuery(id+"F0.wireOp",EDGE,"E2.3.10.3"),sQuery(id+"F0.wireOp",EDGE,"E2.3.11.0"),sQuery(id+"F0.wireOp",EDGE,"E2.3.11.1"),sQuery(id+"F0.wireOp",EDGE,"E2.3.11.2"),sQuery(id+"F0.wireOp",EDGE,"E2.3.11.3"),sQuery(id+"F0.wireOp",EDGE,"E2.3.12.0"),sQuery(id+"F0.wireOp",EDGE,"E2.3.12.1"),sQuery(id+"F0.wireOp",EDGE,"E2.3.12.2"),sQuery(id+"F0.wireOp",EDGE,"E2.3.12.3"),sQuery(id+"F0.wireOp",EDGE,"E2.3.13.0"),sQuery(id+"F0.wireOp",EDGE,"E2.3.13.1"),sQuery(id+"F0.wireOp",EDGE,"E2.3.13.2"),sQuery(id+"F0.wireOp",EDGE,"E2.3.13.3"),sQuery(id+"F0.wireOp",EDGE,"E2.3.14.0"),sQuery(id+"F0.wireOp",EDGE,"E2.3.14.1"),sQuery(id+"F0.wireOp",EDGE,"E2.3.14.2"),sQuery(id+"F0.wireOp",EDGE,"E2.3.14.3"),sQuery(id+"F0.wireOp",EDGE,"E2.3.15.0"),sQuery(id+"F0.wireOp",EDGE,"E2.3.15.1"),sQuery(id+"F0.wireOp",EDGE,"E2.3.15.2"),sQuery(id+"F0.wireOp",EDGE,"E2.3.15.3"),sQuery(id+"F0.wireOp",EDGE,"E2.3.16.0"),sQuery(id+"F0.wireOp",EDGE,"E2.3.16.1"),sQuery(id+"F0.wireOp",EDGE,"E2.3.16.2"),sQuery(id+"F0.wireOp",EDGE,"E2.3.16.3"),sQuery(id+"F0.wireOp",EDGE,"E2.3.17.0"),sQuery(id+"F0.wireOp",EDGE,"E2.3.17.1"),sQuery(id+"F0.wireOp",EDGE,"E2.3.17.2"),sQuery(id+"F0.wireOp",EDGE,"E2.3.17.3"),sQuery(id+"F0.wireOp",EDGE,"E2.3.18.0"),sQuery(id+"F0.wireOp",EDGE,"E2.3.18.1"),sQuery(id+"F0.wireOp",EDGE,"E2.3.18.2"),sQuery(id+"F0.wireOp",EDGE,"E2.3.18.3"),sQuery(id+"F0.wireOp",EDGE,"E2.3.19.0"),sQuery(id+"F0.wireOp",EDGE,"E2.3.19.1"),sQuery(id+"F0.wireOp",EDGE,"E2.3.19.2"),sQuery(id+"F0.wireOp",EDGE,"E2.3.19.3"),sQuery(id+"F0.wireOp",EDGE,"E2.3.20.0"),sQuery(id+"F0.wireOp",EDGE,"E2.3.20.1"),sQuery(id+"F0.wireOp",EDGE,"E2.3.20.2"),sQuery(id+"F0.wireOp",EDGE,"E2.3.20.3"),sQuery(id+"F0.wireOp",EDGE,"E2.3.21.0"),sQuery(id+"F0.wireOp",EDGE,"E2.3.21.1"),sQuery(id+"F0.wireOp",EDGE,"E2.3.21.2"),sQuery(id+"F0.wireOp",EDGE,"E2.3.21.3"),sQuery(id+"F0.wireOp",EDGE,"E2.3.22.0"),sQuery(id+"F0.wireOp",EDGE,"E2.3.22.1"),sQuery(id+"F0.wireOp",EDGE,"E2.3.22.2"),sQuery(id+"F0.wireOp",EDGE,"E2.3.22.3"),sQuery(id+"F0.wireOp",EDGE,"E2.3.23.0"),sQuery(id+"F0.wireOp",EDGE,"E2.3.23.1"),sQuery(id+"F0.wireOp",EDGE,"E2.3.23.2"),sQuery(id+"F0.wireOp",EDGE,"E2.3.23.3"),sQuery(id+"F0.wireOp",EDGE,"E2.3.24.0"),sQuery(id+"F0.wireOp",EDGE,"E2.3.24.1"),sQuery(id+"F0.wireOp",EDGE,"E2.3.24.2"),sQuery(id+"F0.wireOp",EDGE,"E2.3.24.3"),sQuery(id+"F0.wireOp",EDGE,"E2.3.25.0"),sQuery(id+"F0.wireOp",EDGE,"E2.3.25.1"),sQuery(id+"F0.wireOp",EDGE,"E2.3.25.2"),sQuery(id+"F0.wireOp",EDGE,"E2.3.25.3"),sQuery(id+"F0.wireOp",EDGE,"E2.4.0.0"),sQuery(id+"F0.wireOp",EDGE,"E2.4.0.1"),sQuery(id+"F0.wireOp",EDGE,"E2.4.0.2"),sQuery(id+"F0.wireOp",EDGE,"E2.4.0.3"),sQuery(id+"F0.wireOp",EDGE,"E2.4.1.0"),sQuery(id+"F0.wireOp",EDGE,"E2.4.1.1"),sQuery(id+"F0.wireOp",EDGE,"E2.4.1.2"),sQuery(id+"F0.wireOp",EDGE,"E2.4.1.3"),sQuery(id+"F0.wireOp",EDGE,"E2.4.2.0"),sQuery(id+"F0.wireOp",EDGE,"E2.4.2.1"),sQuery(id+"F0.wireOp",EDGE,"E2.4.2.2"),sQuery(id+"F0.wireOp",EDGE,"E2.4.2.3"),sQuery(id+"F0.wireOp",EDGE,"E2.4.3.0"),sQuery(id+"F0.wireOp",EDGE,"E2.4.3.1"),sQuery(id+"F0.wireOp",EDGE,"E2.4.3.2"),sQuery(id+"F0.wireOp",EDGE,"E2.4.3.3"),sQuery(id+"F0.wireOp",EDGE,"E2.4.4.0"),sQuery(id+"F0.wireOp",EDGE,"E2.4.4.1"),sQuery(id+"F0.wireOp",EDGE,"E2.4.4.2"),sQuery(id+"F0.wireOp",EDGE,"E2.4.4.3"),sQuery(id+"F0.wireOp",EDGE,"E2.4.5.0"),sQuery(id+"F0.wireOp",EDGE,"E2.4.5.1"),sQuery(id+"F0.wireOp",EDGE,"E2.4.5.2"),sQuery(id+"F0.wireOp",EDGE,"E2.4.5.3"),sQuery(id+"F0.wireOp",EDGE,"E2.4.6.0"),sQuery(id+"F0.wireOp",EDGE,"E2.4.6.1"),sQuery(id+"F0.wireOp",EDGE,"E2.4.6.2"),sQuery(id+"F0.wireOp",EDGE,"E2.4.6.3"),sQuery(id+"F0.wireOp",EDGE,"E2.4.7.0"),sQuery(id+"F0.wireOp",EDGE,"E2.4.7.1"),sQuery(id+"F0.wireOp",EDGE,"E2.4.7.2"),sQuery(id+"F0.wireOp",EDGE,"E2.4.7.3"),sQuery(id+"F0.wireOp",EDGE,"E2.4.8.0"),sQuery(id+"F0.wireOp",EDGE,"E2.4.8.1"),sQuery(id+"F0.wireOp",EDGE,"E2.4.8.2"),sQuery(id+"F0.wireOp",EDGE,"E2.4.8.3"),sQuery(id+"F0.wireOp",EDGE,"E2.4.9.0"),sQuery(id+"F0.wireOp",EDGE,"E2.4.9.1"),sQuery(id+"F0.wireOp",EDGE,"E2.4.9.2"),sQuery(id+"F0.wireOp",EDGE,"E2.4.9.3"),sQuery(id+"F0.wireOp",EDGE,"E2.4.10.0"),sQuery(id+"F0.wireOp",EDGE,"E2.4.10.1"),sQuery(id+"F0.wireOp",EDGE,"E2.4.10.2"),sQuery(id+"F0.wireOp",EDGE,"E2.4.10.3"),sQuery(id+"F0.wireOp",EDGE,"E2.4.11.0"),sQuery(id+"F0.wireOp",EDGE,"E2.4.11.1"),sQuery(id+"F0.wireOp",EDGE,"E2.4.11.2"),sQuery(id+"F0.wireOp",EDGE,"E2.4.11.3"),sQuery(id+"F0.wireOp",EDGE,"E2.4.12.0"),sQuery(id+"F0.wireOp",EDGE,"E2.4.12.1"),sQuery(id+"F0.wireOp",EDGE,"E2.4.12.2"),sQuery(id+"F0.wireOp",EDGE,"E2.4.12.3"),sQuery(id+"F0.wireOp",EDGE,"E2.4.13.0"),sQuery(id+"F0.wireOp",EDGE,"E2.4.13.1"),sQuery(id+"F0.wireOp",EDGE,"E2.4.13.2"),sQuery(id+"F0.wireOp",EDGE,"E2.4.13.3"),sQuery(id+"F0.wireOp",EDGE,"E2.4.14.0"),sQuery(id+"F0.wireOp",EDGE,"E2.4.14.1"),sQuery(id+"F0.wireOp",EDGE,"E2.4.14.2"),sQuery(id+"F0.wireOp",EDGE,"E2.4.14.3"),sQuery(id+"F0.wireOp",EDGE,"E2.4.15.0"),sQuery(id+"F0.wireOp",EDGE,"E2.4.15.1"),sQuery(id+"F0.wireOp",EDGE,"E2.4.15.2"),sQuery(id+"F0.wireOp",EDGE,"E2.4.15.3"),sQuery(id+"F0.wireOp",EDGE,"E2.4.16.0"),sQuery(id+"F0.wireOp",EDGE,"E2.4.16.1"),sQuery(id+"F0.wireOp",EDGE,"E2.4.16.2"),sQuery(id+"F0.wireOp",EDGE,"E2.4.16.3"),sQuery(id+"F0.wireOp",EDGE,"E2.4.17.0"),sQuery(id+"F0.wireOp",EDGE,"E2.4.17.1"),sQuery(id+"F0.wireOp",EDGE,"E2.4.17.2"),sQuery(id+"F0.wireOp",EDGE,"E2.4.17.3"),sQuery(id+"F0.wireOp",EDGE,"E2.4.18.0"),sQuery(id+"F0.wireOp",EDGE,"E2.4.18.1"),sQuery(id+"F0.wireOp",EDGE,"E2.4.18.2"),sQuery(id+"F0.wireOp",EDGE,"E2.4.18.3"),sQuery(id+"F0.wireOp",EDGE,"E2.4.19.0"),sQuery(id+"F0.wireOp",EDGE,"E2.4.19.1"),sQuery(id+"F0.wireOp",EDGE,"E2.4.19.2"),sQuery(id+"F0.wireOp",EDGE,"E2.4.19.3"),sQuery(id+"F0.wireOp",EDGE,"E2.4.20.0"),sQuery(id+"F0.wireOp",EDGE,"E2.4.20.1"),sQuery(id+"F0.wireOp",EDGE,"E2.4.20.2"),sQuery(id+"F0.wireOp",EDGE,"E2.4.20.3"),sQuery(id+"F0.wireOp",EDGE,"E2.4.21.0"),sQuery(id+"F0.wireOp",EDGE,"E2.4.21.1"),sQuery(id+"F0.wireOp",EDGE,"E2.4.21.2"),sQuery(id+"F0.wireOp",EDGE,"E2.4.21.3"),sQuery(id+"F0.wireOp",EDGE,"E2.4.22.0"),sQuery(id+"F0.wireOp",EDGE,"E2.4.22.1"),sQuery(id+"F0.wireOp",EDGE,"E2.4.22.2"),sQuery(id+"F0.wireOp",EDGE,"E2.4.22.3"),sQuery(id+"F0.wireOp",EDGE,"E2.4.23.0"),sQuery(id+"F0.wireOp",EDGE,"E2.4.23.1"),sQuery(id+"F0.wireOp",EDGE,"E2.4.23.2"),sQuery(id+"F0.wireOp",EDGE,"E2.4.23.3"),sQuery(id+"F0.wireOp",EDGE,"E2.4.24.0"),sQuery(id+"F0.wireOp",EDGE,"E2.4.24.1"),sQuery(id+"F0.wireOp",EDGE,"E2.4.24.2"),sQuery(id+"F0.wireOp",EDGE,"E2.4.24.3"),sQuery(id+"F0.wireOp",EDGE,"E2.4.25.0"),sQuery(id+"F0.wireOp",EDGE,"E2.4.25.1"),sQuery(id+"F0.wireOp",EDGE,"E2.4.25.2"),sQuery(id+"F0.wireOp",EDGE,"E2.4.25.3")])],"isStart":true}),makeQuery(id+"F3.opExtrude","CAP_FACE",FACE,{"disambiguationData":[OSD([sQuery(id+"F2.wireOp",EDGE,"E5.0"),sQuery(id+"F2.wireOp",EDGE,"E6.0"),sQuery(id+"F2.wireOp",EDGE,"E7.0"),sQuery(id+"F2.wireOp",EDGE,"E8.0")])],"isStart":true})]});
            var sketch = newSketch(context, id + "F6", { "sketchPlane" : qUnion([Q0])});
            skLineSegment(sketch, "E10.0", {"start": v(30.46, 42.56) * mm, "end": v(-30.46, 42.56) * mm});
            skLineSegment(sketch, "E11.0", {"start": v(30.46, -42.56) * mm, "end": v(30.46, 42.56) * mm});
            skLineSegment(sketch, "E12.0", {"start": v(30.46, -42.56) * mm, "end": v(-30.46, -42.56) * mm});
            skLineSegment(sketch, "E13.0", {"start": v(-30.46, -42.56) * mm, "end": v(-30.46, 42.56) * mm});
            skLineSegment(sketch, "E14.0", {"start": v(33.46, 45.56) * mm, "end": v(-33.46, 45.56) * mm});
            skLineSegment(sketch, "E14.1", {"start": v(33.46, -45.56) * mm, "end": v(33.46, 45.56) * mm});
            skLineSegment(sketch, "E14.2", {"start": v(33.46, -45.56) * mm, "end": v(-33.46, -45.56) * mm});
            skLineSegment(sketch, "E14.3", {"start": v(-33.46, -45.56) * mm, "end": v(-33.46, 45.56) * mm});
            skSolve(sketch);
        }
        {
            var Q0;
            Q0 = qSketchRegion(id + "F6", true);
            extrude(context, id + "F7", {"entities" : qUnion([Q0]), "operationType" : NewBodyOperationType.ADD, "oppositeDirection" : true, "depth" : .3 * mm});
        }
    });
